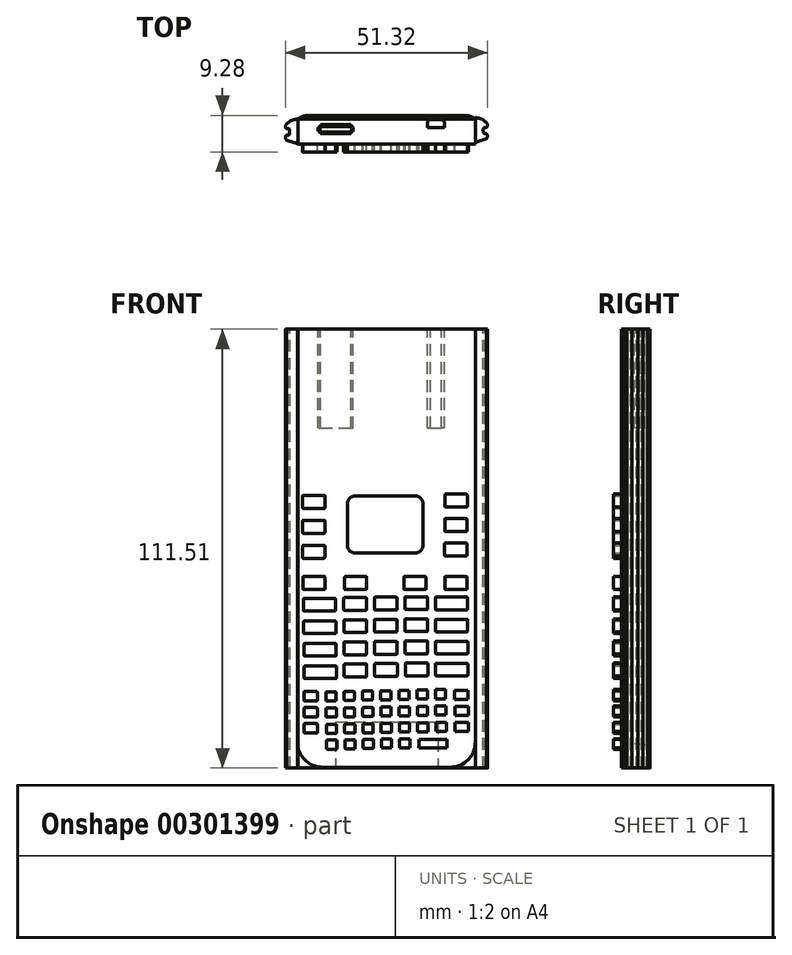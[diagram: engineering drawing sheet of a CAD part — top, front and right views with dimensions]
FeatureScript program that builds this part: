
annotation { "Feature Type Name" : "Feature", "Feature Type Description" : "" }
export const myFeature = defineFeature(function(context is Context, id is Id, definition is map)
    precondition{}
    {
        {
            var Q0;
            Q0=qCreatedBy(makeId("Front.planeOp"),FACE);
            var sketch = newSketch(context, id + "F0", { "sketchPlane" : qUnion([Q0])});
            skLineSegment(sketch, "E0.bottom", {"start": v(-48.38, 55.78) * mm, "end": v(-2.66, 55.78) * mm});
            skLineSegment(sketch, "E0.top", {"start": v(-42.03, -56.6) * mm, "end": v(-9.01, -56.6) * mm});
            skPoint(sketch, "E1.visualSharp", {"position": v(-48.38, -56.6) * mm});
            skPoint(sketch, "E2.visualSharp", {"position": v(-2.66, -56.6) * mm});
            skLineSegment(sketch, "E3.bottom", {"start": v(-36.13, -13.22) * mm, "end": v(-30.79, -13.22) * mm});
            skLineSegment(sketch, "E3.top", {"start": v(-36.13, -16.5) * mm, "end": v(-30.79, -16.5) * mm});
            skLineSegment(sketch, "E3.left", {"start": v(-36.33, -13.42) * mm, "end": v(-36.33, -16.3) * mm});
            skLineSegment(sketch, "E3.right", {"start": v(-30.59, -13.42) * mm, "end": v(-30.59, -16.3) * mm});
            skLineSegment(sketch, "E4.1.0.0", {"start": v(-28.37, -13.1) * mm, "end": v(-23.04, -13.1) * mm});
            skLineSegment(sketch, "E4.1.0.1", {"start": v(-28.57, -13.3) * mm, "end": v(-28.57, -16.2) * mm});
            skLineSegment(sketch, "E4.1.0.2", {"start": v(-28.37, -16.4) * mm, "end": v(-23.04, -16.4) * mm});
            skLineSegment(sketch, "E4.1.0.3", {"start": v(-22.83, -13.3) * mm, "end": v(-22.83, -16.2) * mm});
            skLineSegment(sketch, "E4.2.0.0", {"start": v(-20.62, -13) * mm, "end": v(-15.28, -13) * mm});
            skLineSegment(sketch, "E4.2.0.1", {"start": v(-20.82, -13.2) * mm, "end": v(-20.82, -16.08) * mm});
            skLineSegment(sketch, "E4.2.0.2", {"start": v(-20.62, -16.28) * mm, "end": v(-15.28, -16.28) * mm});
            skLineSegment(sketch, "E4.2.0.3", {"start": v(-15.08, -13.2) * mm, "end": v(-15.08, -16.08) * mm});
            skLineSegment(sketch, "E5.1.0.0", {"start": v(-30.55, -19.04) * mm, "end": v(-30.55, -21.92) * mm});
            skLineSegment(sketch, "E5.1.0.1", {"start": v(-36.1, -18.83) * mm, "end": v(-30.76, -18.83) * mm});
            skLineSegment(sketch, "E5.1.0.2", {"start": v(-36.3, -19.04) * mm, "end": v(-36.3, -21.92) * mm});
            skLineSegment(sketch, "E5.1.0.3", {"start": v(-36.1, -22.12) * mm, "end": v(-30.76, -22.12) * mm});
            skLineSegment(sketch, "E5.2.0.0", {"start": v(-30.52, -24.65) * mm, "end": v(-30.52, -27.53) * mm});
            skLineSegment(sketch, "E5.2.0.1", {"start": v(-36.06, -24.45) * mm, "end": v(-30.72, -24.45) * mm});
            skLineSegment(sketch, "E5.2.0.2", {"start": v(-36.26, -24.65) * mm, "end": v(-36.26, -27.53) * mm});
            skLineSegment(sketch, "E5.2.0.3", {"start": v(-36.06, -27.74) * mm, "end": v(-30.72, -27.74) * mm});
            skLineSegment(sketch, "E5.3.0.0", {"start": v(-30.49, -30.26) * mm, "end": v(-30.49, -33.15) * mm});
            skLineSegment(sketch, "E5.3.0.1", {"start": v(-36.03, -30.06) * mm, "end": v(-30.7, -30.06) * mm});
            skLineSegment(sketch, "E5.3.0.2", {"start": v(-36.23, -30.26) * mm, "end": v(-36.23, -33.15) * mm});
            skLineSegment(sketch, "E5.3.0.3", {"start": v(-36.03, -33.35) * mm, "end": v(-30.7, -33.35) * mm});
            skLineSegment(sketch, "E6.1.0.0", {"start": v(-28.55, -18.9) * mm, "end": v(-28.55, -21.8) * mm});
            skLineSegment(sketch, "E6.1.0.1", {"start": v(-28.35, -18.7) * mm, "end": v(-23.01, -18.7) * mm});
            skLineSegment(sketch, "E6.1.0.2", {"start": v(-22.8, -18.9) * mm, "end": v(-22.8, -21.8) * mm});
            skLineSegment(sketch, "E6.1.0.3", {"start": v(-28.35, -22) * mm, "end": v(-23.01, -22) * mm});
            skLineSegment(sketch, "E6.2.0.0", {"start": v(-20.8, -18.78) * mm, "end": v(-20.8, -21.67) * mm});
            skLineSegment(sketch, "E6.2.0.1", {"start": v(-20.6, -18.58) * mm, "end": v(-15.26, -18.58) * mm});
            skLineSegment(sketch, "E6.2.0.2", {"start": v(-15.06, -18.78) * mm, "end": v(-15.06, -21.67) * mm});
            skLineSegment(sketch, "E6.2.0.3", {"start": v(-20.6, -21.87) * mm, "end": v(-15.26, -21.87) * mm});
            skLineSegment(sketch, "E7.1.0.0", {"start": v(-22.76, -24.52) * mm, "end": v(-22.76, -27.4) * mm});
            skLineSegment(sketch, "E7.1.0.1", {"start": v(-28.3, -24.32) * mm, "end": v(-22.96, -24.32) * mm});
            skLineSegment(sketch, "E7.1.0.2", {"start": v(-28.5, -24.52) * mm, "end": v(-28.5, -27.4) * mm});
            skLineSegment(sketch, "E7.1.0.3", {"start": v(-28.3, -27.6) * mm, "end": v(-22.96, -27.6) * mm});
            skLineSegment(sketch, "E7.1.0.4", {"start": v(-22.72, -30.14) * mm, "end": v(-22.72, -33.02) * mm});
            skLineSegment(sketch, "E7.1.0.5", {"start": v(-28.26, -29.93) * mm, "end": v(-22.93, -29.93) * mm});
            skLineSegment(sketch, "E7.1.0.6", {"start": v(-28.47, -30.14) * mm, "end": v(-28.47, -33.02) * mm});
            skLineSegment(sketch, "E7.1.0.7", {"start": v(-28.26, -33.22) * mm, "end": v(-22.93, -33.22) * mm});
            skLineSegment(sketch, "E7.2.0.0", {"start": v(-15, -24.4) * mm, "end": v(-15, -27.28) * mm});
            skLineSegment(sketch, "E7.2.0.1", {"start": v(-20.53, -24.2) * mm, "end": v(-15.2, -24.2) * mm});
            skLineSegment(sketch, "E7.2.0.2", {"start": v(-20.73, -24.4) * mm, "end": v(-20.73, -27.28) * mm});
            skLineSegment(sketch, "E7.2.0.3", {"start": v(-20.53, -27.48) * mm, "end": v(-15.2, -27.48) * mm});
            skLineSegment(sketch, "E7.2.0.4", {"start": v(-14.96, -30) * mm, "end": v(-14.96, -32.9) * mm});
            skLineSegment(sketch, "E7.2.0.5", {"start": v(-20.5, -29.8) * mm, "end": v(-15.16, -29.8) * mm});
            skLineSegment(sketch, "E7.2.0.6", {"start": v(-20.7, -30) * mm, "end": v(-20.7, -32.9) * mm});
            skLineSegment(sketch, "E7.2.0.7", {"start": v(-20.5, -33.1) * mm, "end": v(-15.16, -33.1) * mm});
            skPoint(sketch, "E8.visualSharp", {"position": v(-30.59, -13.22) * mm});
            skArc(sketch, "E8.filletArc", {"start": v(-30.59, -13.42) * mm, "mid": v(-30.65, -13.28) * mm, "end": v(-30.79, -13.22) * mm});
            skPoint(sketch, "E9.visualSharp", {"position": v(-36.33, -13.22) * mm});
            skArc(sketch, "E9.filletArc", {"start": v(-36.13, -13.22) * mm, "mid": v(-36.27, -13.28) * mm, "end": v(-36.33, -13.42) * mm});
            skPoint(sketch, "E10.visualSharp", {"position": v(-36.33, -16.5) * mm});
            skArc(sketch, "E10.filletArc", {"start": v(-36.33, -16.3) * mm, "mid": v(-36.27, -16.45) * mm, "end": v(-36.13, -16.5) * mm});
            skPoint(sketch, "E11.visualSharp", {"position": v(-30.59, -16.5) * mm});
            skArc(sketch, "E11.filletArc", {"start": v(-30.79, -16.5) * mm, "mid": v(-30.65, -16.45) * mm, "end": v(-30.59, -16.3) * mm});
            skPoint(sketch, "E12.visualSharp", {"position": v(-28.57, -13.1) * mm});
            skArc(sketch, "E12.filletArc", {"start": v(-28.37, -13.1) * mm, "mid": v(-28.52, -13.17) * mm, "end": v(-28.57, -13.3) * mm});
            skPoint(sketch, "E13.visualSharp", {"position": v(-22.83, -13.1) * mm});
            skArc(sketch, "E13.filletArc", {"start": v(-22.83, -13.3) * mm, "mid": v(-22.9, -13.17) * mm, "end": v(-23.04, -13.1) * mm});
            skPoint(sketch, "E14.visualSharp", {"position": v(-22.83, -16.4) * mm});
            skArc(sketch, "E14.filletArc", {"start": v(-23.04, -16.4) * mm, "mid": v(-22.9, -16.34) * mm, "end": v(-22.83, -16.2) * mm});
            skPoint(sketch, "E15.visualSharp", {"position": v(-28.57, -16.4) * mm});
            skArc(sketch, "E15.filletArc", {"start": v(-28.57, -16.2) * mm, "mid": v(-28.52, -16.34) * mm, "end": v(-28.37, -16.4) * mm});
            skPoint(sketch, "E16.visualSharp", {"position": v(-20.82, -13) * mm});
            skArc(sketch, "E16.filletArc", {"start": v(-20.62, -13) * mm, "mid": v(-20.76, -13.05) * mm, "end": v(-20.82, -13.2) * mm});
            skPoint(sketch, "E17.visualSharp", {"position": v(-15.08, -13) * mm});
            skArc(sketch, "E17.filletArc", {"start": v(-15.08, -13.2) * mm, "mid": v(-15.14, -13.05) * mm, "end": v(-15.28, -13) * mm});
            skPoint(sketch, "E18.visualSharp", {"position": v(-15.08, -16.28) * mm});
            skArc(sketch, "E18.filletArc", {"start": v(-15.28, -16.28) * mm, "mid": v(-15.14, -16.22) * mm, "end": v(-15.08, -16.08) * mm});
            skPoint(sketch, "E19.visualSharp", {"position": v(-20.82, -16.28) * mm});
            skArc(sketch, "E19.filletArc", {"start": v(-20.82, -16.08) * mm, "mid": v(-20.76, -16.22) * mm, "end": v(-20.62, -16.28) * mm});
            skPoint(sketch, "E20.visualSharp", {"position": v(-15.06, -18.58) * mm});
            skArc(sketch, "E20.filletArc", {"start": v(-15.06, -18.78) * mm, "mid": v(-15.12, -18.64) * mm, "end": v(-15.26, -18.58) * mm});
            skPoint(sketch, "E21.visualSharp", {"position": v(-15.06, -21.87) * mm});
            skArc(sketch, "E21.filletArc", {"start": v(-15.26, -21.87) * mm, "mid": v(-15.12, -21.81) * mm, "end": v(-15.06, -21.67) * mm});
            skPoint(sketch, "E22.visualSharp", {"position": v(-20.8, -21.87) * mm});
            skArc(sketch, "E22.filletArc", {"start": v(-20.8, -21.67) * mm, "mid": v(-20.74, -21.81) * mm, "end": v(-20.6, -21.87) * mm});
            skPoint(sketch, "E23.visualSharp", {"position": v(-20.8, -18.58) * mm});
            skArc(sketch, "E23.filletArc", {"start": v(-20.6, -18.58) * mm, "mid": v(-20.74, -18.64) * mm, "end": v(-20.8, -18.78) * mm});
            skPoint(sketch, "E24.visualSharp", {"position": v(-22.8, -18.7) * mm});
            skArc(sketch, "E24.filletArc", {"start": v(-22.8, -18.9) * mm, "mid": v(-22.87, -18.77) * mm, "end": v(-23.01, -18.7) * mm});
            skPoint(sketch, "E25.visualSharp", {"position": v(-22.8, -22) * mm});
            skArc(sketch, "E25.filletArc", {"start": v(-23.01, -22) * mm, "mid": v(-22.87, -21.94) * mm, "end": v(-22.8, -21.8) * mm});
            skPoint(sketch, "E26.visualSharp", {"position": v(-28.55, -22) * mm});
            skArc(sketch, "E26.filletArc", {"start": v(-28.55, -21.8) * mm, "mid": v(-28.5, -21.94) * mm, "end": v(-28.35, -22) * mm});
            skPoint(sketch, "E27.visualSharp", {"position": v(-28.55, -18.7) * mm});
            skArc(sketch, "E27.filletArc", {"start": v(-28.35, -18.7) * mm, "mid": v(-28.5, -18.77) * mm, "end": v(-28.55, -18.9) * mm});
            skPoint(sketch, "E28.visualSharp", {"position": v(-30.55, -18.83) * mm});
            skArc(sketch, "E28.filletArc", {"start": v(-30.55, -19.04) * mm, "mid": v(-30.61, -18.9) * mm, "end": v(-30.76, -18.83) * mm});
            skPoint(sketch, "E29.visualSharp", {"position": v(-30.55, -22.12) * mm});
            skArc(sketch, "E29.filletArc", {"start": v(-30.76, -22.12) * mm, "mid": v(-30.61, -22.06) * mm, "end": v(-30.55, -21.92) * mm});
            skPoint(sketch, "E30.visualSharp", {"position": v(-36.3, -22.12) * mm});
            skArc(sketch, "E30.filletArc", {"start": v(-36.3, -21.92) * mm, "mid": v(-36.24, -22.06) * mm, "end": v(-36.1, -22.12) * mm});
            skPoint(sketch, "E31.visualSharp", {"position": v(-36.3, -18.83) * mm});
            skArc(sketch, "E31.filletArc", {"start": v(-36.1, -18.83) * mm, "mid": v(-36.24, -18.9) * mm, "end": v(-36.3, -19.04) * mm});
            skPoint(sketch, "E32.visualSharp", {"position": v(-36.26, -24.45) * mm});
            skArc(sketch, "E32.filletArc", {"start": v(-36.06, -24.45) * mm, "mid": v(-36.2, -24.5) * mm, "end": v(-36.26, -24.65) * mm});
            skPoint(sketch, "E33.visualSharp", {"position": v(-36.26, -27.74) * mm});
            skArc(sketch, "E33.filletArc", {"start": v(-36.26, -27.53) * mm, "mid": v(-36.2, -27.68) * mm, "end": v(-36.06, -27.74) * mm});
            skPoint(sketch, "E34.visualSharp", {"position": v(-30.52, -27.74) * mm});
            skArc(sketch, "E34.filletArc", {"start": v(-30.72, -27.74) * mm, "mid": v(-30.58, -27.68) * mm, "end": v(-30.52, -27.53) * mm});
            skPoint(sketch, "E35.visualSharp", {"position": v(-30.52, -24.45) * mm});
            skArc(sketch, "E35.filletArc", {"start": v(-30.52, -24.65) * mm, "mid": v(-30.58, -24.5) * mm, "end": v(-30.72, -24.45) * mm});
            skPoint(sketch, "E36.visualSharp", {"position": v(-28.5, -24.32) * mm});
            skArc(sketch, "E36.filletArc", {"start": v(-28.3, -24.32) * mm, "mid": v(-28.44, -24.38) * mm, "end": v(-28.5, -24.52) * mm});
            skPoint(sketch, "E37.visualSharp", {"position": v(-22.76, -24.32) * mm});
            skArc(sketch, "E37.filletArc", {"start": v(-22.76, -24.52) * mm, "mid": v(-22.82, -24.38) * mm, "end": v(-22.96, -24.32) * mm});
            skPoint(sketch, "E38.visualSharp", {"position": v(-28.5, -27.6) * mm});
            skArc(sketch, "E38.filletArc", {"start": v(-28.5, -27.4) * mm, "mid": v(-28.44, -27.55) * mm, "end": v(-28.3, -27.6) * mm});
            skPoint(sketch, "E39.visualSharp", {"position": v(-36.23, -30.06) * mm});
            skArc(sketch, "E39.filletArc", {"start": v(-36.03, -30.06) * mm, "mid": v(-36.17, -30.12) * mm, "end": v(-36.23, -30.26) * mm});
            skPoint(sketch, "E40.visualSharp", {"position": v(-36.23, -33.35) * mm});
            skArc(sketch, "E40.filletArc", {"start": v(-36.23, -33.15) * mm, "mid": v(-36.17, -33.3) * mm, "end": v(-36.03, -33.35) * mm});
            skPoint(sketch, "E41.visualSharp", {"position": v(-30.49, -33.35) * mm});
            skArc(sketch, "E41.filletArc", {"start": v(-30.7, -33.35) * mm, "mid": v(-30.55, -33.3) * mm, "end": v(-30.49, -33.15) * mm});
            skPoint(sketch, "E42.visualSharp", {"position": v(-30.49, -30.06) * mm});
            skArc(sketch, "E42.filletArc", {"start": v(-30.49, -30.26) * mm, "mid": v(-30.55, -30.12) * mm, "end": v(-30.7, -30.06) * mm});
            skPoint(sketch, "E43.visualSharp", {"position": v(-28.47, -29.93) * mm});
            skArc(sketch, "E43.filletArc", {"start": v(-28.26, -29.93) * mm, "mid": v(-28.4, -30) * mm, "end": v(-28.47, -30.14) * mm});
            skPoint(sketch, "E44.visualSharp", {"position": v(-28.47, -33.22) * mm});
            skArc(sketch, "E44.filletArc", {"start": v(-28.47, -33.02) * mm, "mid": v(-28.4, -33.16) * mm, "end": v(-28.26, -33.22) * mm});
            skPoint(sketch, "E45.visualSharp", {"position": v(-22.72, -29.93) * mm});
            skArc(sketch, "E45.filletArc", {"start": v(-22.72, -30.14) * mm, "mid": v(-22.78, -30) * mm, "end": v(-22.93, -29.93) * mm});
            skPoint(sketch, "E46.visualSharp", {"position": v(-20.7, -29.8) * mm});
            skArc(sketch, "E46.filletArc", {"start": v(-20.5, -29.8) * mm, "mid": v(-20.64, -29.87) * mm, "end": v(-20.7, -30) * mm});
            skPoint(sketch, "E47.visualSharp", {"position": v(-14.96, -29.8) * mm});
            skArc(sketch, "E47.filletArc", {"start": v(-14.96, -30) * mm, "mid": v(-15.02, -29.87) * mm, "end": v(-15.16, -29.8) * mm});
            skPoint(sketch, "E48.visualSharp", {"position": v(-14.96, -33.1) * mm});
            skArc(sketch, "E48.filletArc", {"start": v(-15.16, -33.1) * mm, "mid": v(-15.02, -33.04) * mm, "end": v(-14.96, -32.9) * mm});
            skPoint(sketch, "E49.visualSharp", {"position": v(-20.7, -33.1) * mm});
            skArc(sketch, "E49.filletArc", {"start": v(-20.7, -32.9) * mm, "mid": v(-20.64, -33.04) * mm, "end": v(-20.5, -33.1) * mm});
            skPoint(sketch, "E50.visualSharp", {"position": v(-20.73, -27.48) * mm});
            skArc(sketch, "E50.filletArc", {"start": v(-20.73, -27.28) * mm, "mid": v(-20.67, -27.42) * mm, "end": v(-20.53, -27.48) * mm});
            skPoint(sketch, "E51.visualSharp", {"position": v(-20.73, -24.2) * mm});
            skArc(sketch, "E51.filletArc", {"start": v(-20.53, -24.2) * mm, "mid": v(-20.67, -24.25) * mm, "end": v(-20.73, -24.4) * mm});
            skPoint(sketch, "E52.visualSharp", {"position": v(-15, -24.2) * mm});
            skArc(sketch, "E52.filletArc", {"start": v(-15, -24.4) * mm, "mid": v(-15.05, -24.25) * mm, "end": v(-15.2, -24.2) * mm});
            skPoint(sketch, "E53.visualSharp", {"position": v(-15, -27.48) * mm});
            skArc(sketch, "E53.filletArc", {"start": v(-15.2, -27.48) * mm, "mid": v(-15.05, -27.42) * mm, "end": v(-15, -27.28) * mm});
            skPoint(sketch, "E54.visualSharp", {"position": v(-22.76, -27.6) * mm});
            skArc(sketch, "E54.filletArc", {"start": v(-22.96, -27.6) * mm, "mid": v(-22.82, -27.55) * mm, "end": v(-22.76, -27.4) * mm});
            skPoint(sketch, "E55.visualSharp", {"position": v(-22.72, -33.22) * mm});
            skArc(sketch, "E55.filletArc", {"start": v(-22.93, -33.22) * mm, "mid": v(-22.78, -33.16) * mm, "end": v(-22.72, -33.02) * mm});
            skLineSegment(sketch, "E56.bottom", {"start": v(-46.4, -13.46) * mm, "end": v(-38.59, -13.46) * mm});
            skLineSegment(sketch, "E56.top", {"start": v(-46.4, -16.64) * mm, "end": v(-38.59, -16.64) * mm});
            skLineSegment(sketch, "E56.left", {"start": v(-46.6, -13.66) * mm, "end": v(-46.6, -16.44) * mm});
            skLineSegment(sketch, "E56.right", {"start": v(-38.39, -13.66) * mm, "end": v(-38.39, -16.44) * mm});
            skLineSegment(sketch, "E57.1.0.0", {"start": v(-46.33, -19.18) * mm, "end": v(-38.51, -19.18) * mm});
            skLineSegment(sketch, "E57.1.0.1", {"start": v(-46.53, -19.38) * mm, "end": v(-46.53, -22.16) * mm});
            skLineSegment(sketch, "E57.1.0.2", {"start": v(-46.33, -22.36) * mm, "end": v(-38.51, -22.36) * mm});
            skLineSegment(sketch, "E57.1.0.3", {"start": v(-38.31, -19.38) * mm, "end": v(-38.31, -22.16) * mm});
            skLineSegment(sketch, "E57.2.0.0", {"start": v(-46.25, -24.9) * mm, "end": v(-38.44, -24.9) * mm});
            skLineSegment(sketch, "E57.2.0.1", {"start": v(-46.46, -25.1) * mm, "end": v(-46.46, -27.88) * mm});
            skLineSegment(sketch, "E57.2.0.2", {"start": v(-46.25, -28.08) * mm, "end": v(-38.44, -28.08) * mm});
            skLineSegment(sketch, "E57.2.0.3", {"start": v(-38.23, -25.1) * mm, "end": v(-38.23, -27.88) * mm});
            skLineSegment(sketch, "E57.3.0.0", {"start": v(-46.18, -30.61) * mm, "end": v(-38.36, -30.61) * mm});
            skLineSegment(sketch, "E57.3.0.1", {"start": v(-46.38, -30.82) * mm, "end": v(-46.38, -33.6) * mm});
            skLineSegment(sketch, "E57.3.0.2", {"start": v(-46.18, -33.8) * mm, "end": v(-38.36, -33.8) * mm});
            skLineSegment(sketch, "E57.3.0.3", {"start": v(-38.16, -30.82) * mm, "end": v(-38.16, -33.6) * mm});
            skLineSegment(sketch, "E58.1.0.0", {"start": v(-12.88, -13.1) * mm, "end": v(-5.06, -13.1) * mm});
            skLineSegment(sketch, "E58.1.0.1", {"start": v(-13.08, -13.3) * mm, "end": v(-13.08, -16.09) * mm});
            skLineSegment(sketch, "E58.1.0.2", {"start": v(-12.88, -16.3) * mm, "end": v(-5.06, -16.3) * mm});
            skLineSegment(sketch, "E58.1.0.3", {"start": v(-4.86, -13.3) * mm, "end": v(-4.86, -16.09) * mm});
            skLineSegment(sketch, "E59.1.0.0", {"start": v(-13.06, -18.91) * mm, "end": v(-13.06, -21.7) * mm});
            skLineSegment(sketch, "E59.1.0.1", {"start": v(-12.85, -18.7) * mm, "end": v(-5.04, -18.7) * mm});
            skLineSegment(sketch, "E59.1.0.2", {"start": v(-4.83, -18.91) * mm, "end": v(-4.83, -21.7) * mm});
            skLineSegment(sketch, "E59.1.0.3", {"start": v(-12.85, -21.9) * mm, "end": v(-5.04, -21.9) * mm});
            skLineSegment(sketch, "E59.2.0.0", {"start": v(-13.03, -24.52) * mm, "end": v(-13.03, -27.3) * mm});
            skLineSegment(sketch, "E59.2.0.1", {"start": v(-12.83, -24.31) * mm, "end": v(-5.01, -24.31) * mm});
            skLineSegment(sketch, "E59.2.0.2", {"start": v(-4.8, -24.52) * mm, "end": v(-4.8, -27.3) * mm});
            skLineSegment(sketch, "E59.2.0.3", {"start": v(-12.83, -27.5) * mm, "end": v(-5.01, -27.5) * mm});
            skLineSegment(sketch, "E59.3.0.0", {"start": v(-13, -30.12) * mm, "end": v(-13, -32.9) * mm});
            skLineSegment(sketch, "E59.3.0.1", {"start": v(-12.8, -29.92) * mm, "end": v(-4.99, -29.92) * mm});
            skLineSegment(sketch, "E59.3.0.2", {"start": v(-4.78, -30.12) * mm, "end": v(-4.78, -32.9) * mm});
            skLineSegment(sketch, "E59.3.0.3", {"start": v(-12.8, -33.1) * mm, "end": v(-4.99, -33.1) * mm});
            skPoint(sketch, "E60.visualSharp", {"position": v(-13.08, -13.1) * mm});
            skArc(sketch, "E60.filletArc", {"start": v(-12.88, -13.1) * mm, "mid": v(-13.02, -13.17) * mm, "end": v(-13.08, -13.3) * mm});
            skPoint(sketch, "E61.visualSharp", {"position": v(-4.86, -13.1) * mm});
            skArc(sketch, "E61.filletArc", {"start": v(-4.86, -13.3) * mm, "mid": v(-4.92, -13.17) * mm, "end": v(-5.06, -13.1) * mm});
            skPoint(sketch, "E62.visualSharp", {"position": v(-4.86, -16.3) * mm});
            skArc(sketch, "E62.filletArc", {"start": v(-5.06, -16.3) * mm, "mid": v(-4.92, -16.23) * mm, "end": v(-4.86, -16.09) * mm});
            skPoint(sketch, "E63.visualSharp", {"position": v(-13.08, -16.3) * mm});
            skArc(sketch, "E63.filletArc", {"start": v(-13.08, -16.09) * mm, "mid": v(-13.02, -16.23) * mm, "end": v(-12.88, -16.3) * mm});
            skPoint(sketch, "E64.visualSharp", {"position": v(-13.06, -18.7) * mm});
            skArc(sketch, "E64.filletArc", {"start": v(-12.85, -18.7) * mm, "mid": v(-13, -18.77) * mm, "end": v(-13.06, -18.91) * mm});
            skPoint(sketch, "E65.visualSharp", {"position": v(-13.06, -21.9) * mm});
            skArc(sketch, "E65.filletArc", {"start": v(-13.06, -21.7) * mm, "mid": v(-13, -21.84) * mm, "end": v(-12.85, -21.9) * mm});
            skPoint(sketch, "E66.visualSharp", {"position": v(-4.83, -21.9) * mm});
            skArc(sketch, "E66.filletArc", {"start": v(-5.04, -21.9) * mm, "mid": v(-4.9, -21.84) * mm, "end": v(-4.83, -21.7) * mm});
            skPoint(sketch, "E67.visualSharp", {"position": v(-4.83, -18.7) * mm});
            skArc(sketch, "E67.filletArc", {"start": v(-4.83, -18.91) * mm, "mid": v(-4.9, -18.77) * mm, "end": v(-5.04, -18.7) * mm});
            skPoint(sketch, "E68.visualSharp", {"position": v(-4.8, -24.31) * mm});
            skArc(sketch, "E68.filletArc", {"start": v(-4.8, -24.52) * mm, "mid": v(-4.87, -24.37) * mm, "end": v(-5.01, -24.31) * mm});
            skPoint(sketch, "E69.visualSharp", {"position": v(-13.03, -24.31) * mm});
            skArc(sketch, "E69.filletArc", {"start": v(-12.83, -24.31) * mm, "mid": v(-12.97, -24.37) * mm, "end": v(-13.03, -24.52) * mm});
            skPoint(sketch, "E70.visualSharp", {"position": v(-13.03, -27.5) * mm});
            skArc(sketch, "E70.filletArc", {"start": v(-13.03, -27.3) * mm, "mid": v(-12.97, -27.44) * mm, "end": v(-12.83, -27.5) * mm});
            skPoint(sketch, "E71.visualSharp", {"position": v(-4.8, -27.5) * mm});
            skArc(sketch, "E71.filletArc", {"start": v(-5.01, -27.5) * mm, "mid": v(-4.87, -27.44) * mm, "end": v(-4.8, -27.3) * mm});
            skPoint(sketch, "E72.visualSharp", {"position": v(-4.78, -29.92) * mm});
            skArc(sketch, "E72.filletArc", {"start": v(-4.78, -30.12) * mm, "mid": v(-4.84, -29.98) * mm, "end": v(-4.99, -29.92) * mm});
            skPoint(sketch, "E73.visualSharp", {"position": v(-13, -29.92) * mm});
            skArc(sketch, "E73.filletArc", {"start": v(-12.8, -29.92) * mm, "mid": v(-12.95, -29.98) * mm, "end": v(-13, -30.12) * mm});
            skPoint(sketch, "E74.visualSharp", {"position": v(-4.78, -33.1) * mm});
            skArc(sketch, "E74.filletArc", {"start": v(-4.99, -33.1) * mm, "mid": v(-4.84, -33.04) * mm, "end": v(-4.78, -32.9) * mm});
            skPoint(sketch, "E75.visualSharp", {"position": v(-13, -33.1) * mm});
            skArc(sketch, "E75.filletArc", {"start": v(-13, -32.9) * mm, "mid": v(-12.95, -33.04) * mm, "end": v(-12.8, -33.1) * mm});
            skPoint(sketch, "E76.visualSharp", {"position": v(-46.6, -13.46) * mm});
            skArc(sketch, "E76.filletArc", {"start": v(-46.4, -13.46) * mm, "mid": v(-46.55, -13.52) * mm, "end": v(-46.6, -13.66) * mm});
            skPoint(sketch, "E77.visualSharp", {"position": v(-38.39, -13.46) * mm});
            skArc(sketch, "E77.filletArc", {"start": v(-38.39, -13.66) * mm, "mid": v(-38.45, -13.52) * mm, "end": v(-38.59, -13.46) * mm});
            skPoint(sketch, "E78.visualSharp", {"position": v(-38.39, -16.64) * mm});
            skArc(sketch, "E78.filletArc", {"start": v(-38.59, -16.64) * mm, "mid": v(-38.45, -16.58) * mm, "end": v(-38.39, -16.44) * mm});
            skPoint(sketch, "E79.visualSharp", {"position": v(-46.53, -19.18) * mm});
            skArc(sketch, "E79.filletArc", {"start": v(-46.33, -19.18) * mm, "mid": v(-46.47, -19.24) * mm, "end": v(-46.53, -19.38) * mm});
            skPoint(sketch, "E80.visualSharp", {"position": v(-46.6, -16.64) * mm});
            skArc(sketch, "E80.filletArc", {"start": v(-46.6, -16.44) * mm, "mid": v(-46.55, -16.58) * mm, "end": v(-46.4, -16.64) * mm});
            skPoint(sketch, "E81.visualSharp", {"position": v(-38.31, -19.18) * mm});
            skArc(sketch, "E81.filletArc", {"start": v(-38.31, -19.38) * mm, "mid": v(-38.37, -19.24) * mm, "end": v(-38.51, -19.18) * mm});
            skPoint(sketch, "E82.visualSharp", {"position": v(-38.31, -22.36) * mm});
            skArc(sketch, "E82.filletArc", {"start": v(-38.51, -22.36) * mm, "mid": v(-38.37, -22.3) * mm, "end": v(-38.31, -22.16) * mm});
            skPoint(sketch, "E83.visualSharp", {"position": v(-46.53, -22.36) * mm});
            skArc(sketch, "E83.filletArc", {"start": v(-46.53, -22.16) * mm, "mid": v(-46.47, -22.3) * mm, "end": v(-46.33, -22.36) * mm});
            skPoint(sketch, "E84.visualSharp", {"position": v(-46.46, -24.9) * mm});
            skArc(sketch, "E84.filletArc", {"start": v(-46.25, -24.9) * mm, "mid": v(-46.4, -24.96) * mm, "end": v(-46.46, -25.1) * mm});
            skPoint(sketch, "E85.visualSharp", {"position": v(-38.23, -24.9) * mm});
            skArc(sketch, "E85.filletArc", {"start": v(-38.23, -25.1) * mm, "mid": v(-38.3, -24.96) * mm, "end": v(-38.44, -24.9) * mm});
            skPoint(sketch, "E86.visualSharp", {"position": v(-38.23, -28.08) * mm});
            skArc(sketch, "E86.filletArc", {"start": v(-38.44, -28.08) * mm, "mid": v(-38.3, -28.02) * mm, "end": v(-38.23, -27.88) * mm});
            skPoint(sketch, "E87.visualSharp", {"position": v(-46.46, -28.08) * mm});
            skArc(sketch, "E87.filletArc", {"start": v(-46.46, -27.88) * mm, "mid": v(-46.4, -28.02) * mm, "end": v(-46.25, -28.08) * mm});
            skPoint(sketch, "E88.visualSharp", {"position": v(-46.38, -30.61) * mm});
            skArc(sketch, "E88.filletArc", {"start": v(-46.18, -30.61) * mm, "mid": v(-46.32, -30.67) * mm, "end": v(-46.38, -30.82) * mm});
            skPoint(sketch, "E89.visualSharp", {"position": v(-38.16, -30.61) * mm});
            skArc(sketch, "E89.filletArc", {"start": v(-38.16, -30.82) * mm, "mid": v(-38.22, -30.67) * mm, "end": v(-38.36, -30.61) * mm});
            skPoint(sketch, "E90.visualSharp", {"position": v(-38.16, -33.8) * mm});
            skArc(sketch, "E90.filletArc", {"start": v(-38.36, -33.8) * mm, "mid": v(-38.22, -33.74) * mm, "end": v(-38.16, -33.6) * mm});
            skPoint(sketch, "E91.visualSharp", {"position": v(-46.38, -33.8) * mm});
            skArc(sketch, "E91.filletArc", {"start": v(-46.38, -33.6) * mm, "mid": v(-46.32, -33.74) * mm, "end": v(-46.18, -33.8) * mm});
            skLineSegment(sketch, "E92.bottom", {"start": v(-46.58, 12.78) * mm, "end": v(-41.3, 12.78) * mm});
            skLineSegment(sketch, "E92.top", {"start": v(-46.58, 9.49) * mm, "end": v(-41.3, 9.49) * mm});
            skLineSegment(sketch, "E92.left", {"start": v(-46.79, 12.58) * mm, "end": v(-46.79, 9.7) * mm});
            skLineSegment(sketch, "E92.right", {"start": v(-41.1, 12.58) * mm, "end": v(-41.1, 9.7) * mm});
            skLineSegment(sketch, "E93.1.0.0", {"start": v(-41.12, 6.23) * mm, "end": v(-41.12, 3.34) * mm});
            skLineSegment(sketch, "E93.1.0.1", {"start": v(-46.61, 6.43) * mm, "end": v(-41.33, 6.43) * mm});
            skLineSegment(sketch, "E93.1.0.2", {"start": v(-46.81, 6.23) * mm, "end": v(-46.81, 3.34) * mm});
            skLineSegment(sketch, "E93.1.0.3", {"start": v(-46.61, 3.14) * mm, "end": v(-41.33, 3.14) * mm});
            skLineSegment(sketch, "E93.2.0.0", {"start": v(-41.15, -0.12) * mm, "end": v(-41.15, -3) * mm});
            skLineSegment(sketch, "E93.2.0.1", {"start": v(-46.64, 0.08) * mm, "end": v(-41.35, 0.08) * mm});
            skLineSegment(sketch, "E93.2.0.2", {"start": v(-46.84, -0.12) * mm, "end": v(-46.84, -3) * mm});
            skLineSegment(sketch, "E93.2.0.3", {"start": v(-46.64, -3.21) * mm, "end": v(-41.35, -3.21) * mm});
            skLineSegment(sketch, "E94.1.0.0", {"start": v(-10.44, 13.06) * mm, "end": v(-5.16, 13.06) * mm});
            skLineSegment(sketch, "E94.1.0.1", {"start": v(-10.64, 12.85) * mm, "end": v(-10.64, 9.96) * mm});
            skLineSegment(sketch, "E94.1.0.2", {"start": v(-10.44, 9.76) * mm, "end": v(-5.16, 9.76) * mm});
            skLineSegment(sketch, "E94.1.0.3", {"start": v(-4.95, 12.85) * mm, "end": v(-4.95, 9.96) * mm});
            skLineSegment(sketch, "E95.1.0.0", {"start": v(-10.67, 6.65) * mm, "end": v(-10.67, 3.76) * mm});
            skLineSegment(sketch, "E95.1.0.1", {"start": v(-10.46, 6.85) * mm, "end": v(-5.18, 6.85) * mm});
            skLineSegment(sketch, "E95.1.0.2", {"start": v(-4.98, 6.65) * mm, "end": v(-4.98, 3.76) * mm});
            skLineSegment(sketch, "E95.1.0.3", {"start": v(-10.46, 3.56) * mm, "end": v(-5.18, 3.56) * mm});
            skLineSegment(sketch, "E95.2.0.0", {"start": v(-10.7, 0.44) * mm, "end": v(-10.7, -2.44) * mm});
            skLineSegment(sketch, "E95.2.0.1", {"start": v(-10.5, 0.65) * mm, "end": v(-5.2, 0.65) * mm});
            skLineSegment(sketch, "E95.2.0.2", {"start": v(-5, 0.44) * mm, "end": v(-5, -2.44) * mm});
            skLineSegment(sketch, "E95.2.0.3", {"start": v(-10.5, -2.65) * mm, "end": v(-5.2, -2.65) * mm});
            skLineSegment(sketch, "E96.1.0.0", {"start": v(-10.46, -7.87) * mm, "end": v(-5.18, -7.87) * mm});
            skLineSegment(sketch, "E96.1.0.1", {"start": v(-10.67, -8.08) * mm, "end": v(-10.67, -10.97) * mm});
            skLineSegment(sketch, "E96.1.0.2", {"start": v(-10.46, -11.17) * mm, "end": v(-5.18, -11.17) * mm});
            skLineSegment(sketch, "E96.1.0.3", {"start": v(-4.98, -8.08) * mm, "end": v(-4.98, -10.97) * mm});
            skLineSegment(sketch, "E97.1.0.0", {"start": v(-21.08, -8.08) * mm, "end": v(-21.08, -10.97) * mm});
            skLineSegment(sketch, "E97.1.0.1", {"start": v(-20.88, -7.88) * mm, "end": v(-15.6, -7.88) * mm});
            skLineSegment(sketch, "E97.1.0.2", {"start": v(-15.4, -8.08) * mm, "end": v(-15.4, -10.97) * mm});
            skLineSegment(sketch, "E97.1.0.3", {"start": v(-20.88, -11.18) * mm, "end": v(-15.6, -11.18) * mm});
            skLineSegment(sketch, "E98.1.0.0", {"start": v(-46.53, -7.87) * mm, "end": v(-41.25, -7.87) * mm});
            skLineSegment(sketch, "E98.1.0.1", {"start": v(-46.53, -11.17) * mm, "end": v(-41.25, -11.17) * mm});
            skLineSegment(sketch, "E98.1.0.2", {"start": v(-41.05, -8.08) * mm, "end": v(-41.05, -10.97) * mm});
            skLineSegment(sketch, "E98.1.0.3", {"start": v(-46.74, -8.08) * mm, "end": v(-46.74, -10.97) * mm});
            skLineSegment(sketch, "E99.1.0.0", {"start": v(-30.48, -8.08) * mm, "end": v(-30.48, -10.97) * mm});
            skLineSegment(sketch, "E99.1.0.1", {"start": v(-35.97, -7.88) * mm, "end": v(-30.68, -7.88) * mm});
            skLineSegment(sketch, "E99.1.0.2", {"start": v(-36.17, -8.08) * mm, "end": v(-36.17, -10.97) * mm});
            skLineSegment(sketch, "E99.1.0.3", {"start": v(-35.97, -11.18) * mm, "end": v(-30.68, -11.18) * mm});
            skPoint(sketch, "E100.visualSharp", {"position": v(-46.79, 12.78) * mm});
            skArc(sketch, "E100.filletArc", {"start": v(-46.58, 12.78) * mm, "mid": v(-46.73, 12.72) * mm, "end": v(-46.79, 12.58) * mm});
            skPoint(sketch, "E101.visualSharp", {"position": v(-41.1, 12.78) * mm});
            skArc(sketch, "E101.filletArc", {"start": v(-41.1, 12.58) * mm, "mid": v(-41.16, 12.72) * mm, "end": v(-41.3, 12.78) * mm});
            skPoint(sketch, "E102.visualSharp", {"position": v(-46.79, 9.49) * mm});
            skArc(sketch, "E102.filletArc", {"start": v(-46.79, 9.7) * mm, "mid": v(-46.73, 9.55) * mm, "end": v(-46.58, 9.49) * mm});
            skPoint(sketch, "E103.visualSharp", {"position": v(-41.1, 9.49) * mm});
            skArc(sketch, "E103.filletArc", {"start": v(-41.3, 9.49) * mm, "mid": v(-41.16, 9.55) * mm, "end": v(-41.1, 9.7) * mm});
            skPoint(sketch, "E104.visualSharp", {"position": v(-41.12, 6.43) * mm});
            skArc(sketch, "E104.filletArc", {"start": v(-41.12, 6.23) * mm, "mid": v(-41.18, 6.38) * mm, "end": v(-41.33, 6.43) * mm});
            skPoint(sketch, "E105.visualSharp", {"position": v(-46.81, 6.43) * mm});
            skArc(sketch, "E105.filletArc", {"start": v(-46.61, 6.43) * mm, "mid": v(-46.75, 6.38) * mm, "end": v(-46.81, 6.23) * mm});
            skPoint(sketch, "E106.visualSharp", {"position": v(-46.81, 3.14) * mm});
            skArc(sketch, "E106.filletArc", {"start": v(-46.81, 3.34) * mm, "mid": v(-46.75, 3.2) * mm, "end": v(-46.61, 3.14) * mm});
            skPoint(sketch, "E107.visualSharp", {"position": v(-41.12, 3.14) * mm});
            skArc(sketch, "E107.filletArc", {"start": v(-41.33, 3.14) * mm, "mid": v(-41.18, 3.2) * mm, "end": v(-41.12, 3.34) * mm});
            skPoint(sketch, "E108.visualSharp", {"position": v(-41.15, 0.08) * mm});
            skArc(sketch, "E108.filletArc", {"start": v(-41.15, -0.12) * mm, "mid": v(-41.2, 0.03) * mm, "end": v(-41.35, 0.08) * mm});
            skPoint(sketch, "E109.visualSharp", {"position": v(-46.84, 0.08) * mm});
            skArc(sketch, "E109.filletArc", {"start": v(-46.64, 0.08) * mm, "mid": v(-46.78, 0.03) * mm, "end": v(-46.84, -0.12) * mm});
            skPoint(sketch, "E110.visualSharp", {"position": v(-46.84, -3.21) * mm});
            skArc(sketch, "E110.filletArc", {"start": v(-46.84, -3) * mm, "mid": v(-46.78, -3.15) * mm, "end": v(-46.64, -3.21) * mm});
            skPoint(sketch, "E111.visualSharp", {"position": v(-41.15, -3.21) * mm});
            skArc(sketch, "E111.filletArc", {"start": v(-41.35, -3.21) * mm, "mid": v(-41.2, -3.15) * mm, "end": v(-41.15, -3) * mm});
            skPoint(sketch, "E112.visualSharp", {"position": v(-41.05, -7.87) * mm});
            skArc(sketch, "E112.filletArc", {"start": v(-41.05, -8.08) * mm, "mid": v(-41.1, -7.93) * mm, "end": v(-41.25, -7.87) * mm});
            skPoint(sketch, "E113.visualSharp", {"position": v(-41.05, -11.17) * mm});
            skArc(sketch, "E113.filletArc", {"start": v(-41.25, -11.17) * mm, "mid": v(-41.1, -11.11) * mm, "end": v(-41.05, -10.97) * mm});
            skPoint(sketch, "E114.visualSharp", {"position": v(-46.74, -11.17) * mm});
            skArc(sketch, "E114.filletArc", {"start": v(-46.74, -10.97) * mm, "mid": v(-46.68, -11.11) * mm, "end": v(-46.53, -11.17) * mm});
            skPoint(sketch, "E115.visualSharp", {"position": v(-46.74, -7.87) * mm});
            skArc(sketch, "E115.filletArc", {"start": v(-46.53, -7.87) * mm, "mid": v(-46.68, -7.93) * mm, "end": v(-46.74, -8.08) * mm});
            skPoint(sketch, "E116.visualSharp", {"position": v(-36.17, -7.88) * mm});
            skArc(sketch, "E116.filletArc", {"start": v(-35.97, -7.88) * mm, "mid": v(-36.11, -7.94) * mm, "end": v(-36.17, -8.08) * mm});
            skPoint(sketch, "E117.visualSharp", {"position": v(-30.48, -11.18) * mm});
            skArc(sketch, "E117.filletArc", {"start": v(-30.68, -11.18) * mm, "mid": v(-30.54, -11.12) * mm, "end": v(-30.48, -10.97) * mm});
            skPoint(sketch, "E118.visualSharp", {"position": v(-36.17, -11.18) * mm});
            skArc(sketch, "E118.filletArc", {"start": v(-36.17, -10.97) * mm, "mid": v(-36.11, -11.12) * mm, "end": v(-35.97, -11.18) * mm});
            skPoint(sketch, "E119.visualSharp", {"position": v(-30.48, -7.88) * mm});
            skArc(sketch, "E119.filletArc", {"start": v(-30.48, -8.08) * mm, "mid": v(-30.54, -7.94) * mm, "end": v(-30.68, -7.88) * mm});
            skPoint(sketch, "E120.visualSharp", {"position": v(-21.08, -7.88) * mm});
            skArc(sketch, "E120.filletArc", {"start": v(-20.88, -7.88) * mm, "mid": v(-21.02, -7.94) * mm, "end": v(-21.08, -8.08) * mm});
            skPoint(sketch, "E121.visualSharp", {"position": v(-21.08, -11.18) * mm});
            skArc(sketch, "E121.filletArc", {"start": v(-21.08, -10.97) * mm, "mid": v(-21.02, -11.12) * mm, "end": v(-20.88, -11.18) * mm});
            skPoint(sketch, "E122.visualSharp", {"position": v(-15.4, -11.18) * mm});
            skArc(sketch, "E122.filletArc", {"start": v(-15.6, -11.18) * mm, "mid": v(-15.45, -11.12) * mm, "end": v(-15.4, -10.97) * mm});
            skPoint(sketch, "E123.visualSharp", {"position": v(-15.4, -7.88) * mm});
            skArc(sketch, "E123.filletArc", {"start": v(-15.4, -8.08) * mm, "mid": v(-15.45, -7.94) * mm, "end": v(-15.6, -7.88) * mm});
            skPoint(sketch, "E124.visualSharp", {"position": v(-10.67, -7.87) * mm});
            skArc(sketch, "E124.filletArc", {"start": v(-10.46, -7.87) * mm, "mid": v(-10.6, -7.93) * mm, "end": v(-10.67, -8.08) * mm});
            skPoint(sketch, "E125.visualSharp", {"position": v(-10.67, -11.17) * mm});
            skArc(sketch, "E125.filletArc", {"start": v(-10.67, -10.97) * mm, "mid": v(-10.6, -11.11) * mm, "end": v(-10.46, -11.17) * mm});
            skPoint(sketch, "E126.visualSharp", {"position": v(-4.98, -11.17) * mm});
            skArc(sketch, "E126.filletArc", {"start": v(-5.18, -11.17) * mm, "mid": v(-5.04, -11.11) * mm, "end": v(-4.98, -10.97) * mm});
            skPoint(sketch, "E127.visualSharp", {"position": v(-4.98, -7.87) * mm});
            skArc(sketch, "E127.filletArc", {"start": v(-4.98, -8.08) * mm, "mid": v(-5.04, -7.93) * mm, "end": v(-5.18, -7.87) * mm});
            skPoint(sketch, "E128.visualSharp", {"position": v(-5, -2.65) * mm});
            skArc(sketch, "E128.filletArc", {"start": v(-5.2, -2.65) * mm, "mid": v(-5.06, -2.59) * mm, "end": v(-5, -2.44) * mm});
            skPoint(sketch, "E129.visualSharp", {"position": v(-5, 0.65) * mm});
            skArc(sketch, "E129.filletArc", {"start": v(-5, 0.44) * mm, "mid": v(-5.06, 0.59) * mm, "end": v(-5.2, 0.65) * mm});
            skPoint(sketch, "E130.visualSharp", {"position": v(-10.7, 0.65) * mm});
            skArc(sketch, "E130.filletArc", {"start": v(-10.5, 0.65) * mm, "mid": v(-10.63, 0.59) * mm, "end": v(-10.7, 0.44) * mm});
            skPoint(sketch, "E131.visualSharp", {"position": v(-10.7, -2.65) * mm});
            skArc(sketch, "E131.filletArc", {"start": v(-10.7, -2.44) * mm, "mid": v(-10.63, -2.59) * mm, "end": v(-10.5, -2.65) * mm});
            skPoint(sketch, "E132.visualSharp", {"position": v(-10.67, 3.56) * mm});
            skArc(sketch, "E132.filletArc", {"start": v(-10.67, 3.76) * mm, "mid": v(-10.6, 3.62) * mm, "end": v(-10.46, 3.56) * mm});
            skPoint(sketch, "E133.visualSharp", {"position": v(-10.67, 6.85) * mm});
            skArc(sketch, "E133.filletArc", {"start": v(-10.46, 6.85) * mm, "mid": v(-10.6, 6.8) * mm, "end": v(-10.67, 6.65) * mm});
            skPoint(sketch, "E134.visualSharp", {"position": v(-4.98, 6.85) * mm});
            skArc(sketch, "E134.filletArc", {"start": v(-4.98, 6.65) * mm, "mid": v(-5.04, 6.8) * mm, "end": v(-5.18, 6.85) * mm});
            skPoint(sketch, "E135.visualSharp", {"position": v(-4.98, 3.56) * mm});
            skArc(sketch, "E135.filletArc", {"start": v(-5.18, 3.56) * mm, "mid": v(-5.04, 3.62) * mm, "end": v(-4.98, 3.76) * mm});
            skPoint(sketch, "E136.visualSharp", {"position": v(-4.95, 9.76) * mm});
            skArc(sketch, "E136.filletArc", {"start": v(-5.16, 9.76) * mm, "mid": v(-5.01, 9.82) * mm, "end": v(-4.95, 9.96) * mm});
            skPoint(sketch, "E137.visualSharp", {"position": v(-4.95, 13.06) * mm});
            skArc(sketch, "E137.filletArc", {"start": v(-4.95, 12.85) * mm, "mid": v(-5.01, 13) * mm, "end": v(-5.16, 13.06) * mm});
            skPoint(sketch, "E138.visualSharp", {"position": v(-10.64, 13.06) * mm});
            skArc(sketch, "E138.filletArc", {"start": v(-10.44, 13.06) * mm, "mid": v(-10.58, 13) * mm, "end": v(-10.64, 12.85) * mm});
            skPoint(sketch, "E139.visualSharp", {"position": v(-10.64, 9.76) * mm});
            skArc(sketch, "E139.filletArc", {"start": v(-10.64, 9.96) * mm, "mid": v(-10.58, 9.82) * mm, "end": v(-10.44, 9.76) * mm});
            skLineSegment(sketch, "E140.bottom", {"start": v(-33.37, 12.63) * mm, "end": v(-23.53, 12.63) * mm});
            skLineSegment(sketch, "E140.top", {"start": v(-33.37, -1.92) * mm, "end": v(-18.21, -1.92) * mm});
            skLineSegment(sketch, "E140.left", {"start": v(-35.4, 10.6) * mm, "end": v(-35.4, 0.11) * mm});
            skLineSegment(sketch, "E140.right", {"start": v(-16.18, 10.6) * mm, "end": v(-16.18, 0.11) * mm});
            skPoint(sketch, "E141.visualSharp", {"position": v(-35.4, 12.63) * mm});
            skArc(sketch, "E141.filletArc", {"start": v(-33.37, 12.63) * mm, "mid": v(-34.8, 12.04) * mm, "end": v(-35.4, 10.6) * mm});
            skPoint(sketch, "E142.visualSharp", {"position": v(-16.18, 12.63) * mm});
            skPoint(sketch, "E143.visualSharp", {"position": v(-16.18, 10.6) * mm});
            skArc(sketch, "E143.filletArc", {"start": v(-16.18, 10.6) * mm, "mid": v(-16.77, 12.04) * mm, "end": v(-18.21, 12.63) * mm});
            skLineSegment(sketch, "E144", {"start": v(-23.53, 12.63) * mm, "end": v(-18.21, 12.63) * mm});
            skPoint(sketch, "E145.visualSharp", {"position": v(-35.4, -1.92) * mm});
            skArc(sketch, "E145.filletArc", {"start": v(-35.4, 0.11) * mm, "mid": v(-34.8, -1.32) * mm, "end": v(-33.37, -1.92) * mm});
            skPoint(sketch, "E146.visualSharp", {"position": v(-16.18, -1.92) * mm});
            skArc(sketch, "E146.filletArc", {"start": v(-18.21, -1.92) * mm, "mid": v(-16.77, -1.32) * mm, "end": v(-16.18, 0.11) * mm});
            skLineSegment(sketch, "E147.bottom", {"start": v(-46.26, -37.05) * mm, "end": v(-43.25, -37.05) * mm});
            skLineSegment(sketch, "E147.top", {"start": v(-46.26, -39.51) * mm, "end": v(-43.25, -39.51) * mm});
            skLineSegment(sketch, "E147.left", {"start": v(-46.46, -37.26) * mm, "end": v(-46.46, -39.31) * mm});
            skLineSegment(sketch, "E147.right", {"start": v(-43.05, -37.26) * mm, "end": v(-43.05, -39.31) * mm});
            skLineSegment(sketch, "E148.1.0.0", {"start": v(-46.23, -41.17) * mm, "end": v(-43.22, -41.17) * mm});
            skLineSegment(sketch, "E148.1.0.1", {"start": v(-46.43, -41.38) * mm, "end": v(-46.43, -43.36) * mm});
            skLineSegment(sketch, "E148.1.0.2", {"start": v(-43.02, -41.38) * mm, "end": v(-43.02, -43.36) * mm});
            skLineSegment(sketch, "E148.1.0.3", {"start": v(-46.23, -43.57) * mm, "end": v(-43.22, -43.57) * mm});
            skLineSegment(sketch, "E148.2.0.0", {"start": v(-46.2, -45.23) * mm, "end": v(-43.2, -45.23) * mm});
            skLineSegment(sketch, "E148.2.0.1", {"start": v(-46.4, -45.43) * mm, "end": v(-46.4, -47.42) * mm});
            skLineSegment(sketch, "E148.2.0.2", {"start": v(-43, -45.43) * mm, "end": v(-43, -47.42) * mm});
            skLineSegment(sketch, "E148.2.0.3", {"start": v(-46.2, -47.62) * mm, "end": v(-43.2, -47.62) * mm});
            skLineSegment(sketch, "E149.1.0.0", {"start": v(-4.72, -36.75) * mm, "end": v(-4.72, -39.14) * mm});
            skLineSegment(sketch, "E149.1.0.1", {"start": v(-8.13, -36.75) * mm, "end": v(-4.72, -36.75) * mm});
            skLineSegment(sketch, "E149.1.0.2", {"start": v(-8.13, -36.75) * mm, "end": v(-8.13, -39.14) * mm});
            skLineSegment(sketch, "E149.1.0.3", {"start": v(-8.13, -39.14) * mm, "end": v(-4.72, -39.14) * mm});
            skLineSegment(sketch, "E150.1.0.0", {"start": v(-8.1, -40.81) * mm, "end": v(-8.1, -43.2) * mm});
            skLineSegment(sketch, "E150.1.0.1", {"start": v(-8.1, -40.81) * mm, "end": v(-4.7, -40.81) * mm});
            skLineSegment(sketch, "E150.1.0.2", {"start": v(-4.7, -40.81) * mm, "end": v(-4.7, -43.2) * mm});
            skLineSegment(sketch, "E150.1.0.3", {"start": v(-8.1, -43.2) * mm, "end": v(-4.7, -43.2) * mm});
            skLineSegment(sketch, "E150.2.0.0", {"start": v(-8.07, -44.87) * mm, "end": v(-8.07, -47.27) * mm});
            skLineSegment(sketch, "E150.2.0.1", {"start": v(-8.07, -44.87) * mm, "end": v(-4.66, -44.87) * mm});
            skLineSegment(sketch, "E150.2.0.2", {"start": v(-4.66, -44.87) * mm, "end": v(-4.66, -47.27) * mm});
            skLineSegment(sketch, "E150.2.0.3", {"start": v(-8.07, -47.27) * mm, "end": v(-4.66, -47.27) * mm});
            skLineSegment(sketch, "E151.bottom", {"start": v(-40.66, -37.12) * mm, "end": v(-38.45, -37.12) * mm});
            skLineSegment(sketch, "E151.top", {"start": v(-40.66, -39.43) * mm, "end": v(-38.45, -39.43) * mm});
            skLineSegment(sketch, "E151.left", {"start": v(-40.86, -37.32) * mm, "end": v(-40.86, -39.23) * mm});
            skLineSegment(sketch, "E151.right", {"start": v(-38.25, -37.32) * mm, "end": v(-38.25, -39.23) * mm});
            skLineSegment(sketch, "E152.1.0.0", {"start": v(-36.02, -37.03) * mm, "end": v(-33.81, -37.03) * mm});
            skLineSegment(sketch, "E152.1.0.1", {"start": v(-36.22, -37.24) * mm, "end": v(-36.22, -39.14) * mm});
            skLineSegment(sketch, "E152.1.0.2", {"start": v(-36.02, -39.35) * mm, "end": v(-33.81, -39.35) * mm});
            skLineSegment(sketch, "E152.1.0.3", {"start": v(-33.61, -37.24) * mm, "end": v(-33.61, -39.14) * mm});
            skLineSegment(sketch, "E152.2.0.0", {"start": v(-31.38, -36.95) * mm, "end": v(-29.18, -36.95) * mm});
            skLineSegment(sketch, "E152.2.0.1", {"start": v(-31.58, -37.15) * mm, "end": v(-31.58, -39.06) * mm});
            skLineSegment(sketch, "E152.2.0.2", {"start": v(-31.38, -39.26) * mm, "end": v(-29.18, -39.26) * mm});
            skLineSegment(sketch, "E152.2.0.3", {"start": v(-28.97, -37.15) * mm, "end": v(-28.97, -39.06) * mm});
            skLineSegment(sketch, "E152.3.0.0", {"start": v(-26.74, -36.86) * mm, "end": v(-24.33, -36.86) * mm});
            skLineSegment(sketch, "E152.3.0.1", {"start": v(-26.94, -37.06) * mm, "end": v(-26.94, -39.17) * mm});
            skLineSegment(sketch, "E152.3.0.2", {"start": v(-26.94, -39.17) * mm, "end": v(-24.33, -39.17) * mm});
            skLineSegment(sketch, "E152.3.0.3", {"start": v(-24.33, -36.86) * mm, "end": v(-24.33, -39.17) * mm});
            skLineSegment(sketch, "E152.4.0.0", {"start": v(-22.3, -36.77) * mm, "end": v(-19.7, -36.77) * mm});
            skLineSegment(sketch, "E152.4.0.1", {"start": v(-22.3, -36.77) * mm, "end": v(-22.3, -39.09) * mm});
            skLineSegment(sketch, "E152.4.0.2", {"start": v(-22.3, -39.09) * mm, "end": v(-19.7, -39.09) * mm});
            skLineSegment(sketch, "E152.4.0.3", {"start": v(-19.7, -36.77) * mm, "end": v(-19.7, -39.09) * mm});
            skLineSegment(sketch, "E152.5.0.0", {"start": v(-17.67, -36.69) * mm, "end": v(-15.06, -36.69) * mm});
            skLineSegment(sketch, "E152.5.0.1", {"start": v(-17.67, -36.69) * mm, "end": v(-17.67, -39) * mm});
            skLineSegment(sketch, "E152.5.0.2", {"start": v(-17.67, -39) * mm, "end": v(-15.06, -39) * mm});
            skLineSegment(sketch, "E152.5.0.3", {"start": v(-15.06, -36.69) * mm, "end": v(-15.06, -39) * mm});
            skLineSegment(sketch, "E152.6.0.0", {"start": v(-13.03, -36.6) * mm, "end": v(-10.42, -36.6) * mm});
            skLineSegment(sketch, "E152.6.0.1", {"start": v(-13.03, -36.6) * mm, "end": v(-13.03, -38.91) * mm});
            skLineSegment(sketch, "E152.6.0.2", {"start": v(-13.03, -38.91) * mm, "end": v(-10.42, -38.91) * mm});
            skLineSegment(sketch, "E152.6.0.3", {"start": v(-10.42, -36.6) * mm, "end": v(-10.42, -38.91) * mm});
            skLineSegment(sketch, "E153.1.0.0", {"start": v(-40.8, -41.48) * mm, "end": v(-40.8, -43.38) * mm});
            skLineSegment(sketch, "E153.1.0.1", {"start": v(-40.59, -41.27) * mm, "end": v(-38.39, -41.27) * mm});
            skLineSegment(sketch, "E153.1.0.2", {"start": v(-38.18, -41.48) * mm, "end": v(-38.18, -43.38) * mm});
            skLineSegment(sketch, "E153.1.0.3", {"start": v(-40.59, -43.59) * mm, "end": v(-38.39, -43.59) * mm});
            skLineSegment(sketch, "E153.1.0.4", {"start": v(-36.15, -41.39) * mm, "end": v(-36.15, -43.3) * mm});
            skLineSegment(sketch, "E153.1.0.5", {"start": v(-35.95, -41.19) * mm, "end": v(-33.75, -41.19) * mm});
            skLineSegment(sketch, "E153.1.0.6", {"start": v(-33.54, -41.39) * mm, "end": v(-33.54, -43.3) * mm});
            skLineSegment(sketch, "E153.1.0.7", {"start": v(-35.95, -43.5) * mm, "end": v(-33.75, -43.5) * mm});
            skLineSegment(sketch, "E153.1.0.8", {"start": v(-31.51, -41.3) * mm, "end": v(-31.51, -43.2) * mm});
            skLineSegment(sketch, "E153.1.0.9", {"start": v(-31.31, -41.1) * mm, "end": v(-29.1, -41.1) * mm});
            skLineSegment(sketch, "E153.1.0.10", {"start": v(-28.9, -41.3) * mm, "end": v(-28.9, -43.2) * mm});
            skLineSegment(sketch, "E153.1.0.11", {"start": v(-31.31, -43.41) * mm, "end": v(-29.1, -43.41) * mm});
            skLineSegment(sketch, "E153.1.0.12", {"start": v(-26.88, -41.01) * mm, "end": v(-26.88, -43.33) * mm});
            skLineSegment(sketch, "E153.1.0.13", {"start": v(-26.88, -41.01) * mm, "end": v(-24.27, -41.01) * mm});
            skLineSegment(sketch, "E153.1.0.14", {"start": v(-24.27, -41.01) * mm, "end": v(-24.27, -43.33) * mm});
            skLineSegment(sketch, "E153.1.0.15", {"start": v(-26.88, -43.33) * mm, "end": v(-24.27, -43.33) * mm});
            skLineSegment(sketch, "E153.1.0.16", {"start": v(-22.24, -40.92) * mm, "end": v(-22.24, -43.24) * mm});
            skLineSegment(sketch, "E153.1.0.17", {"start": v(-22.24, -40.92) * mm, "end": v(-19.63, -40.92) * mm});
            skLineSegment(sketch, "E153.1.0.18", {"start": v(-19.63, -40.92) * mm, "end": v(-19.63, -43.24) * mm});
            skLineSegment(sketch, "E153.1.0.19", {"start": v(-22.24, -43.24) * mm, "end": v(-19.63, -43.24) * mm});
            skLineSegment(sketch, "E153.1.0.20", {"start": v(-17.6, -40.84) * mm, "end": v(-17.6, -43.15) * mm});
            skLineSegment(sketch, "E153.1.0.21", {"start": v(-17.6, -40.84) * mm, "end": v(-14.99, -40.84) * mm});
            skLineSegment(sketch, "E153.1.0.22", {"start": v(-14.99, -40.84) * mm, "end": v(-14.99, -43.15) * mm});
            skLineSegment(sketch, "E153.1.0.23", {"start": v(-17.6, -43.15) * mm, "end": v(-14.99, -43.15) * mm});
            skLineSegment(sketch, "E153.1.0.24", {"start": v(-12.96, -40.75) * mm, "end": v(-12.96, -43.06) * mm});
            skLineSegment(sketch, "E153.1.0.25", {"start": v(-12.96, -40.75) * mm, "end": v(-10.35, -40.75) * mm});
            skLineSegment(sketch, "E153.1.0.26", {"start": v(-10.35, -40.75) * mm, "end": v(-10.35, -43.06) * mm});
            skLineSegment(sketch, "E153.1.0.27", {"start": v(-12.96, -43.06) * mm, "end": v(-10.35, -43.06) * mm});
            skLineSegment(sketch, "E153.2.0.0", {"start": v(-40.73, -45.63) * mm, "end": v(-40.73, -47.54) * mm});
            skLineSegment(sketch, "E153.2.0.1", {"start": v(-40.52, -45.42) * mm, "end": v(-38.32, -45.42) * mm});
            skLineSegment(sketch, "E153.2.0.2", {"start": v(-38.12, -45.63) * mm, "end": v(-38.12, -47.54) * mm});
            skLineSegment(sketch, "E153.2.0.3", {"start": v(-40.52, -47.74) * mm, "end": v(-38.32, -47.74) * mm});
            skLineSegment(sketch, "E153.2.0.4", {"start": v(-36.09, -45.54) * mm, "end": v(-36.09, -47.45) * mm});
            skLineSegment(sketch, "E153.2.0.5", {"start": v(-35.88, -45.34) * mm, "end": v(-33.68, -45.34) * mm});
            skLineSegment(sketch, "E153.2.0.6", {"start": v(-33.48, -45.54) * mm, "end": v(-33.48, -47.45) * mm});
            skLineSegment(sketch, "E153.2.0.7", {"start": v(-35.88, -47.65) * mm, "end": v(-33.68, -47.65) * mm});
            skLineSegment(sketch, "E153.2.0.8", {"start": v(-31.45, -45.45) * mm, "end": v(-31.45, -47.36) * mm});
            skLineSegment(sketch, "E153.2.0.9", {"start": v(-31.24, -45.25) * mm, "end": v(-29.04, -45.25) * mm});
            skLineSegment(sketch, "E153.2.0.10", {"start": v(-28.84, -45.45) * mm, "end": v(-28.84, -47.36) * mm});
            skLineSegment(sketch, "E153.2.0.11", {"start": v(-31.24, -47.56) * mm, "end": v(-29.04, -47.56) * mm});
            skLineSegment(sketch, "E153.2.0.12", {"start": v(-26.8, -45.16) * mm, "end": v(-26.8, -47.48) * mm});
            skLineSegment(sketch, "E153.2.0.13", {"start": v(-26.8, -45.16) * mm, "end": v(-24.2, -45.16) * mm});
            skLineSegment(sketch, "E153.2.0.14", {"start": v(-24.2, -45.16) * mm, "end": v(-24.2, -47.48) * mm});
            skLineSegment(sketch, "E153.2.0.15", {"start": v(-26.8, -47.48) * mm, "end": v(-24.2, -47.48) * mm});
            skLineSegment(sketch, "E153.2.0.16", {"start": v(-22.17, -45.08) * mm, "end": v(-22.17, -47.4) * mm});
            skLineSegment(sketch, "E153.2.0.17", {"start": v(-22.17, -45.08) * mm, "end": v(-19.56, -45.08) * mm});
            skLineSegment(sketch, "E153.2.0.18", {"start": v(-19.56, -45.08) * mm, "end": v(-19.56, -47.4) * mm});
            skLineSegment(sketch, "E153.2.0.19", {"start": v(-22.17, -47.4) * mm, "end": v(-19.56, -47.4) * mm});
            skLineSegment(sketch, "E153.2.0.20", {"start": v(-17.53, -44.99) * mm, "end": v(-17.53, -47.3) * mm});
            skLineSegment(sketch, "E153.2.0.21", {"start": v(-17.53, -44.99) * mm, "end": v(-14.92, -44.99) * mm});
            skLineSegment(sketch, "E153.2.0.22", {"start": v(-14.92, -44.99) * mm, "end": v(-14.92, -47.3) * mm});
            skLineSegment(sketch, "E153.2.0.23", {"start": v(-17.53, -47.3) * mm, "end": v(-14.92, -47.3) * mm});
            skLineSegment(sketch, "E153.2.0.24", {"start": v(-12.9, -44.9) * mm, "end": v(-12.9, -47.22) * mm});
            skLineSegment(sketch, "E153.2.0.25", {"start": v(-12.9, -44.9) * mm, "end": v(-10.28, -44.9) * mm});
            skLineSegment(sketch, "E153.2.0.26", {"start": v(-10.28, -44.9) * mm, "end": v(-10.28, -47.22) * mm});
            skLineSegment(sketch, "E153.2.0.27", {"start": v(-12.9, -47.22) * mm, "end": v(-10.28, -47.22) * mm});
            skLineSegment(sketch, "E154.1.0.0", {"start": v(-40.46, -49.4) * mm, "end": v(-38.26, -49.4) * mm});
            skLineSegment(sketch, "E154.1.0.1", {"start": v(-40.67, -49.6) * mm, "end": v(-40.67, -51.51) * mm});
            skLineSegment(sketch, "E154.1.0.2", {"start": v(-40.46, -51.72) * mm, "end": v(-38.26, -51.72) * mm});
            skLineSegment(sketch, "E154.1.0.3", {"start": v(-38.06, -49.6) * mm, "end": v(-38.06, -51.51) * mm});
            skLineSegment(sketch, "E154.1.0.4", {"start": v(-36.03, -49.52) * mm, "end": v(-36.03, -51.43) * mm});
            skLineSegment(sketch, "E154.1.0.5", {"start": v(-35.82, -49.32) * mm, "end": v(-33.62, -49.32) * mm});
            skLineSegment(sketch, "E154.1.0.6", {"start": v(-33.42, -49.52) * mm, "end": v(-33.42, -51.43) * mm});
            skLineSegment(sketch, "E154.1.0.7", {"start": v(-35.82, -51.63) * mm, "end": v(-33.62, -51.63) * mm});
            skLineSegment(sketch, "E154.1.0.8", {"start": v(-31.39, -49.43) * mm, "end": v(-31.39, -51.34) * mm});
            skLineSegment(sketch, "E154.1.0.9", {"start": v(-31.18, -49.23) * mm, "end": v(-28.98, -49.23) * mm});
            skLineSegment(sketch, "E154.1.0.10", {"start": v(-28.78, -49.43) * mm, "end": v(-28.78, -51.34) * mm});
            skLineSegment(sketch, "E154.1.0.11", {"start": v(-31.18, -51.54) * mm, "end": v(-28.98, -51.54) * mm});
            skLineSegment(sketch, "E154.1.0.12", {"start": v(-26.75, -49.14) * mm, "end": v(-26.75, -51.46) * mm});
            skLineSegment(sketch, "E154.1.0.13", {"start": v(-26.75, -49.14) * mm, "end": v(-24.14, -49.14) * mm});
            skLineSegment(sketch, "E154.1.0.14", {"start": v(-24.14, -49.14) * mm, "end": v(-24.14, -51.46) * mm});
            skLineSegment(sketch, "E154.1.0.15", {"start": v(-26.75, -51.46) * mm, "end": v(-24.14, -51.46) * mm});
            skLineSegment(sketch, "E154.1.0.16", {"start": v(-22.11, -49.06) * mm, "end": v(-22.11, -51.37) * mm});
            skLineSegment(sketch, "E154.1.0.17", {"start": v(-22.11, -49.06) * mm, "end": v(-19.5, -49.06) * mm});
            skLineSegment(sketch, "E154.1.0.18", {"start": v(-19.5, -49.06) * mm, "end": v(-19.5, -51.37) * mm});
            skLineSegment(sketch, "E154.1.0.19", {"start": v(-22.11, -51.37) * mm, "end": v(-19.5, -51.37) * mm});
            skLineSegment(sketch, "E155.bottom", {"start": v(-17.19, -49.25) * mm, "end": v(-10.11, -49.25) * mm});
            skLineSegment(sketch, "E155.top", {"start": v(-17.19, -51.43) * mm, "end": v(-10.11, -51.43) * mm});
            skLineSegment(sketch, "E155.left", {"start": v(-17.19, -49.25) * mm, "end": v(-17.19, -51.43) * mm});
            skLineSegment(sketch, "E155.right", {"start": v(-10.11, -49.25) * mm, "end": v(-10.11, -51.43) * mm});
            skPoint(sketch, "E156.visualSharp", {"position": v(-46.46, -37.05) * mm});
            skArc(sketch, "E156.filletArc", {"start": v(-46.26, -37.05) * mm, "mid": v(-46.4, -37.11) * mm, "end": v(-46.46, -37.26) * mm});
            skPoint(sketch, "E157.visualSharp", {"position": v(-43.05, -39.51) * mm});
            skArc(sketch, "E157.filletArc", {"start": v(-43.25, -39.51) * mm, "mid": v(-43.11, -39.45) * mm, "end": v(-43.05, -39.31) * mm});
            skPoint(sketch, "E158.visualSharp", {"position": v(-43.05, -37.05) * mm});
            skArc(sketch, "E158.filletArc", {"start": v(-43.05, -37.26) * mm, "mid": v(-43.11, -37.11) * mm, "end": v(-43.25, -37.05) * mm});
            skPoint(sketch, "E159.visualSharp", {"position": v(-46.46, -39.51) * mm});
            skArc(sketch, "E159.filletArc", {"start": v(-46.46, -39.31) * mm, "mid": v(-46.4, -39.45) * mm, "end": v(-46.26, -39.51) * mm});
            skPoint(sketch, "E160.visualSharp", {"position": v(-40.86, -37.12) * mm});
            skArc(sketch, "E160.filletArc", {"start": v(-40.66, -37.12) * mm, "mid": v(-40.8, -37.18) * mm, "end": v(-40.86, -37.32) * mm});
            skPoint(sketch, "E161.visualSharp", {"position": v(-46.43, -41.17) * mm});
            skArc(sketch, "E161.filletArc", {"start": v(-46.23, -41.17) * mm, "mid": v(-46.37, -41.23) * mm, "end": v(-46.43, -41.38) * mm});
            skPoint(sketch, "E162.visualSharp", {"position": v(-46.43, -43.57) * mm});
            skArc(sketch, "E162.filletArc", {"start": v(-46.43, -43.36) * mm, "mid": v(-46.37, -43.5) * mm, "end": v(-46.23, -43.57) * mm});
            skPoint(sketch, "E163.visualSharp", {"position": v(-46.4, -45.23) * mm});
            skArc(sketch, "E163.filletArc", {"start": v(-46.2, -45.23) * mm, "mid": v(-46.34, -45.29) * mm, "end": v(-46.4, -45.43) * mm});
            skPoint(sketch, "E164.visualSharp", {"position": v(-46.4, -47.62) * mm});
            skArc(sketch, "E164.filletArc", {"start": v(-46.4, -47.42) * mm, "mid": v(-46.34, -47.56) * mm, "end": v(-46.2, -47.62) * mm});
            skPoint(sketch, "E165.visualSharp", {"position": v(-43, -47.62) * mm});
            skArc(sketch, "E165.filletArc", {"start": v(-43.2, -47.62) * mm, "mid": v(-43.05, -47.56) * mm, "end": v(-43, -47.42) * mm});
            skPoint(sketch, "E166.visualSharp", {"position": v(-43, -45.23) * mm});
            skArc(sketch, "E166.filletArc", {"start": v(-43, -45.43) * mm, "mid": v(-43.05, -45.29) * mm, "end": v(-43.2, -45.23) * mm});
            skPoint(sketch, "E167.visualSharp", {"position": v(-43.02, -43.57) * mm});
            skArc(sketch, "E167.filletArc", {"start": v(-43.22, -43.57) * mm, "mid": v(-43.08, -43.5) * mm, "end": v(-43.02, -43.36) * mm});
            skPoint(sketch, "E168.visualSharp", {"position": v(-43.02, -41.17) * mm});
            skArc(sketch, "E168.filletArc", {"start": v(-43.02, -41.38) * mm, "mid": v(-43.08, -41.23) * mm, "end": v(-43.22, -41.17) * mm});
            skPoint(sketch, "E169.visualSharp", {"position": v(-40.86, -39.43) * mm});
            skArc(sketch, "E169.filletArc", {"start": v(-40.86, -39.23) * mm, "mid": v(-40.8, -39.37) * mm, "end": v(-40.66, -39.43) * mm});
            skPoint(sketch, "E170.visualSharp", {"position": v(-40.8, -41.27) * mm});
            skArc(sketch, "E170.filletArc", {"start": v(-40.59, -41.27) * mm, "mid": v(-40.73, -41.33) * mm, "end": v(-40.8, -41.48) * mm});
            skPoint(sketch, "E171.visualSharp", {"position": v(-40.8, -43.59) * mm});
            skArc(sketch, "E171.filletArc", {"start": v(-40.8, -43.38) * mm, "mid": v(-40.73, -43.53) * mm, "end": v(-40.59, -43.59) * mm});
            skPoint(sketch, "E172.visualSharp", {"position": v(-40.73, -45.42) * mm});
            skArc(sketch, "E172.filletArc", {"start": v(-40.52, -45.42) * mm, "mid": v(-40.67, -45.48) * mm, "end": v(-40.73, -45.63) * mm});
            skPoint(sketch, "E173.visualSharp", {"position": v(-40.73, -47.74) * mm});
            skArc(sketch, "E173.filletArc", {"start": v(-40.73, -47.54) * mm, "mid": v(-40.67, -47.68) * mm, "end": v(-40.52, -47.74) * mm});
            skPoint(sketch, "E174.visualSharp", {"position": v(-40.67, -49.4) * mm});
            skArc(sketch, "E174.filletArc", {"start": v(-40.46, -49.4) * mm, "mid": v(-40.6, -49.46) * mm, "end": v(-40.67, -49.6) * mm});
            skPoint(sketch, "E175.visualSharp", {"position": v(-40.67, -51.72) * mm});
            skArc(sketch, "E175.filletArc", {"start": v(-40.67, -51.51) * mm, "mid": v(-40.6, -51.66) * mm, "end": v(-40.46, -51.72) * mm});
            skPoint(sketch, "E176.visualSharp", {"position": v(-38.06, -51.72) * mm});
            skArc(sketch, "E176.filletArc", {"start": v(-38.26, -51.72) * mm, "mid": v(-38.12, -51.66) * mm, "end": v(-38.06, -51.51) * mm});
            skPoint(sketch, "E177.visualSharp", {"position": v(-38.06, -49.4) * mm});
            skArc(sketch, "E177.filletArc", {"start": v(-38.06, -49.6) * mm, "mid": v(-38.12, -49.46) * mm, "end": v(-38.26, -49.4) * mm});
            skPoint(sketch, "E178.visualSharp", {"position": v(-38.12, -47.74) * mm});
            skArc(sketch, "E178.filletArc", {"start": v(-38.32, -47.74) * mm, "mid": v(-38.18, -47.68) * mm, "end": v(-38.12, -47.54) * mm});
            skPoint(sketch, "E179.visualSharp", {"position": v(-38.12, -45.42) * mm});
            skArc(sketch, "E179.filletArc", {"start": v(-38.12, -45.63) * mm, "mid": v(-38.18, -45.48) * mm, "end": v(-38.32, -45.42) * mm});
            skPoint(sketch, "E180.visualSharp", {"position": v(-38.18, -43.59) * mm});
            skArc(sketch, "E180.filletArc", {"start": v(-38.39, -43.59) * mm, "mid": v(-38.24, -43.53) * mm, "end": v(-38.18, -43.38) * mm});
            skPoint(sketch, "E181.visualSharp", {"position": v(-38.18, -41.27) * mm});
            skArc(sketch, "E181.filletArc", {"start": v(-38.18, -41.48) * mm, "mid": v(-38.24, -41.33) * mm, "end": v(-38.39, -41.27) * mm});
            skPoint(sketch, "E182.visualSharp", {"position": v(-38.25, -39.43) * mm});
            skArc(sketch, "E182.filletArc", {"start": v(-38.45, -39.43) * mm, "mid": v(-38.3, -39.37) * mm, "end": v(-38.25, -39.23) * mm});
            skPoint(sketch, "E183.visualSharp", {"position": v(-38.25, -37.12) * mm});
            skArc(sketch, "E183.filletArc", {"start": v(-38.25, -37.32) * mm, "mid": v(-38.3, -37.18) * mm, "end": v(-38.45, -37.12) * mm});
            skPoint(sketch, "E184.visualSharp", {"position": v(-36.22, -37.03) * mm});
            skArc(sketch, "E184.filletArc", {"start": v(-36.02, -37.03) * mm, "mid": v(-36.16, -37.1) * mm, "end": v(-36.22, -37.24) * mm});
            skPoint(sketch, "E185.visualSharp", {"position": v(-36.22, -39.35) * mm});
            skArc(sketch, "E185.filletArc", {"start": v(-36.22, -39.14) * mm, "mid": v(-36.16, -39.29) * mm, "end": v(-36.02, -39.35) * mm});
            skPoint(sketch, "E186.visualSharp", {"position": v(-36.15, -41.19) * mm});
            skArc(sketch, "E186.filletArc", {"start": v(-35.95, -41.19) * mm, "mid": v(-36.1, -41.24) * mm, "end": v(-36.15, -41.39) * mm});
            skPoint(sketch, "E187.visualSharp", {"position": v(-36.15, -43.5) * mm});
            skArc(sketch, "E187.filletArc", {"start": v(-36.15, -43.3) * mm, "mid": v(-36.1, -43.44) * mm, "end": v(-35.95, -43.5) * mm});
            skPoint(sketch, "E188.visualSharp", {"position": v(-36.09, -45.34) * mm});
            skArc(sketch, "E188.filletArc", {"start": v(-35.88, -45.34) * mm, "mid": v(-36.03, -45.4) * mm, "end": v(-36.09, -45.54) * mm});
            skPoint(sketch, "E189.visualSharp", {"position": v(-36.09, -47.65) * mm});
            skArc(sketch, "E189.filletArc", {"start": v(-36.09, -47.45) * mm, "mid": v(-36.03, -47.6) * mm, "end": v(-35.88, -47.65) * mm});
            skPoint(sketch, "E190.visualSharp", {"position": v(-36.03, -49.32) * mm});
            skArc(sketch, "E190.filletArc", {"start": v(-35.82, -49.32) * mm, "mid": v(-35.97, -49.38) * mm, "end": v(-36.03, -49.52) * mm});
            skPoint(sketch, "E191.visualSharp", {"position": v(-36.03, -51.63) * mm});
            skArc(sketch, "E191.filletArc", {"start": v(-36.03, -51.43) * mm, "mid": v(-35.97, -51.57) * mm, "end": v(-35.82, -51.63) * mm});
            skPoint(sketch, "E192.visualSharp", {"position": v(-33.42, -51.63) * mm});
            skArc(sketch, "E192.filletArc", {"start": v(-33.62, -51.63) * mm, "mid": v(-33.48, -51.57) * mm, "end": v(-33.42, -51.43) * mm});
            skPoint(sketch, "E193.visualSharp", {"position": v(-33.42, -49.32) * mm});
            skArc(sketch, "E193.filletArc", {"start": v(-33.42, -49.52) * mm, "mid": v(-33.48, -49.38) * mm, "end": v(-33.62, -49.32) * mm});
            skPoint(sketch, "E194.visualSharp", {"position": v(-33.48, -47.65) * mm});
            skArc(sketch, "E194.filletArc", {"start": v(-33.68, -47.65) * mm, "mid": v(-33.54, -47.6) * mm, "end": v(-33.48, -47.45) * mm});
            skPoint(sketch, "E195.visualSharp", {"position": v(-33.48, -45.34) * mm});
            skArc(sketch, "E195.filletArc", {"start": v(-33.48, -45.54) * mm, "mid": v(-33.54, -45.4) * mm, "end": v(-33.68, -45.34) * mm});
            skPoint(sketch, "E196.visualSharp", {"position": v(-33.54, -43.5) * mm});
            skArc(sketch, "E196.filletArc", {"start": v(-33.75, -43.5) * mm, "mid": v(-33.6, -43.44) * mm, "end": v(-33.54, -43.3) * mm});
            skPoint(sketch, "E197.visualSharp", {"position": v(-33.54, -41.19) * mm});
            skArc(sketch, "E197.filletArc", {"start": v(-33.54, -41.39) * mm, "mid": v(-33.6, -41.24) * mm, "end": v(-33.75, -41.19) * mm});
            skPoint(sketch, "E198.visualSharp", {"position": v(-33.61, -39.35) * mm});
            skArc(sketch, "E198.filletArc", {"start": v(-33.81, -39.35) * mm, "mid": v(-33.67, -39.29) * mm, "end": v(-33.61, -39.14) * mm});
            skPoint(sketch, "E199.visualSharp", {"position": v(-33.61, -37.03) * mm});
            skArc(sketch, "E199.filletArc", {"start": v(-33.61, -37.24) * mm, "mid": v(-33.67, -37.1) * mm, "end": v(-33.81, -37.03) * mm});
            skPoint(sketch, "E200.visualSharp", {"position": v(-31.58, -36.95) * mm});
            skArc(sketch, "E200.filletArc", {"start": v(-31.38, -36.95) * mm, "mid": v(-31.52, -37) * mm, "end": v(-31.58, -37.15) * mm});
            skPoint(sketch, "E201.visualSharp", {"position": v(-31.58, -39.26) * mm});
            skArc(sketch, "E201.filletArc", {"start": v(-31.58, -39.06) * mm, "mid": v(-31.52, -39.2) * mm, "end": v(-31.38, -39.26) * mm});
            skPoint(sketch, "E202.visualSharp", {"position": v(-31.51, -41.1) * mm});
            skArc(sketch, "E202.filletArc", {"start": v(-31.31, -41.1) * mm, "mid": v(-31.46, -41.16) * mm, "end": v(-31.51, -41.3) * mm});
            skPoint(sketch, "E203.visualSharp", {"position": v(-31.51, -43.41) * mm});
            skArc(sketch, "E203.filletArc", {"start": v(-31.51, -43.2) * mm, "mid": v(-31.46, -43.35) * mm, "end": v(-31.31, -43.41) * mm});
            skPoint(sketch, "E204.visualSharp", {"position": v(-31.45, -45.25) * mm});
            skArc(sketch, "E204.filletArc", {"start": v(-31.24, -45.25) * mm, "mid": v(-31.39, -45.31) * mm, "end": v(-31.45, -45.45) * mm});
            skPoint(sketch, "E205.visualSharp", {"position": v(-31.45, -47.56) * mm});
            skArc(sketch, "E205.filletArc", {"start": v(-31.45, -47.36) * mm, "mid": v(-31.39, -47.5) * mm, "end": v(-31.24, -47.56) * mm});
            skPoint(sketch, "E206.visualSharp", {"position": v(-31.39, -49.23) * mm});
            skArc(sketch, "E206.filletArc", {"start": v(-31.18, -49.23) * mm, "mid": v(-31.33, -49.29) * mm, "end": v(-31.39, -49.43) * mm});
            skPoint(sketch, "E207.visualSharp", {"position": v(-31.39, -51.54) * mm});
            skArc(sketch, "E207.filletArc", {"start": v(-31.39, -51.34) * mm, "mid": v(-31.33, -51.48) * mm, "end": v(-31.18, -51.54) * mm});
            skPoint(sketch, "E208.visualSharp", {"position": v(-28.78, -51.54) * mm});
            skArc(sketch, "E208.filletArc", {"start": v(-28.98, -51.54) * mm, "mid": v(-28.84, -51.48) * mm, "end": v(-28.78, -51.34) * mm});
            skPoint(sketch, "E209.visualSharp", {"position": v(-28.78, -49.23) * mm});
            skArc(sketch, "E209.filletArc", {"start": v(-28.78, -49.43) * mm, "mid": v(-28.84, -49.29) * mm, "end": v(-28.98, -49.23) * mm});
            skPoint(sketch, "E210.visualSharp", {"position": v(-28.84, -47.56) * mm});
            skArc(sketch, "E210.filletArc", {"start": v(-29.04, -47.56) * mm, "mid": v(-28.9, -47.5) * mm, "end": v(-28.84, -47.36) * mm});
            skPoint(sketch, "E211.visualSharp", {"position": v(-28.84, -45.25) * mm});
            skArc(sketch, "E211.filletArc", {"start": v(-28.84, -45.45) * mm, "mid": v(-28.9, -45.31) * mm, "end": v(-29.04, -45.25) * mm});
            skPoint(sketch, "E212.visualSharp", {"position": v(-28.9, -43.41) * mm});
            skArc(sketch, "E212.filletArc", {"start": v(-29.1, -43.41) * mm, "mid": v(-28.96, -43.35) * mm, "end": v(-28.9, -43.2) * mm});
            skPoint(sketch, "E213.visualSharp", {"position": v(-28.9, -41.1) * mm});
            skArc(sketch, "E213.filletArc", {"start": v(-28.9, -41.3) * mm, "mid": v(-28.96, -41.16) * mm, "end": v(-29.1, -41.1) * mm});
            skPoint(sketch, "E214.visualSharp", {"position": v(-28.97, -39.26) * mm});
            skArc(sketch, "E214.filletArc", {"start": v(-29.18, -39.26) * mm, "mid": v(-29.03, -39.2) * mm, "end": v(-28.97, -39.06) * mm});
            skPoint(sketch, "E215.visualSharp", {"position": v(-28.97, -36.95) * mm});
            skArc(sketch, "E215.filletArc", {"start": v(-28.97, -37.15) * mm, "mid": v(-29.03, -37) * mm, "end": v(-29.18, -36.95) * mm});
            skPoint(sketch, "E216.visualSharp", {"position": v(-26.94, -36.86) * mm});
            skArc(sketch, "E216.filletArc", {"start": v(-26.74, -36.86) * mm, "mid": v(-26.88, -36.92) * mm, "end": v(-26.94, -37.06) * mm});
            skSolve(sketch);
        }
        {
            var Q0;
            Q0=qCreatedBy(makeId("Front.planeOp"),FACE);
            var sketch = newSketch(context, id + "F1", { "sketchPlane" : qUnion([Q0])});
            skLineSegment(sketch, "E217.bottom", {"start": v(-48.06, 55) * mm, "end": v(-2.9, 55) * mm});
            skLineSegment(sketch, "E217.top", {"start": v(-41.7, -56.32) * mm, "end": v(-9.25, -56.32) * mm});
            skLineSegment(sketch, "E217.left", {"start": v(-48.06, 55) * mm, "end": v(-48.06, -49.97) * mm});
            skLineSegment(sketch, "E217.right", {"start": v(-2.9, 55) * mm, "end": v(-2.9, -49.97) * mm});
            skPoint(sketch, "E218.visualSharp", {"position": v(-48.06, -56.32) * mm});
            skArc(sketch, "E218.filletArc", {"start": v(-48.06, -49.97) * mm, "mid": v(-46.2, -54.46) * mm, "end": v(-41.7, -56.32) * mm});
            skPoint(sketch, "E219.visualSharp", {"position": v(-2.9, -56.32) * mm});
            skArc(sketch, "E219.filletArc", {"start": v(-9.25, -56.32) * mm, "mid": v(-4.76, -54.46) * mm, "end": v(-2.9, -49.97) * mm});
            skSolve(sketch);
        }
        {
            var Q0;
            Q0 = qSketchRegion(id + "F0", true);
            extrude(context, id + "F2", {"entities" : qUnion([Q0]), "depth" : 2 * mm});
        }
        {
            var Q0;
            Q0 = qSketchRegion(id + "F1", true);
            extrude(context, id + "F3", {"entities" : qUnion([Q0]), "oppositeDirection" : true, "depth" : 6.38 * mm});
        }
        {
            var Q0;
            Q0=makeQuery(id+"F3.opExtrude","SWEPT_FACE",FACE,{"disambiguationData":[OSD([sQuery(id+"F1.wireOp",EDGE,"E217.bottom")])]});
            var sketch = newSketch(context, id + "F4", { "sketchPlane" : qUnion([Q0])});
            skLineSegment(sketch, "E220.bottom", {"start": v(-42.3, 4.5) * mm, "end": v(-34.5, 4.46) * mm});
            skLineSegment(sketch, "E220.top", {"start": v(-42.3, 3.16) * mm, "end": v(-34.5, 3.1) * mm});
            skLineSegment(sketch, "E220.left", {"start": v(-42.4, 4.4) * mm, "end": v(-42.4, 3.26) * mm});
            skLineSegment(sketch, "E220.right", {"start": v(-34.4, 4.36) * mm, "end": v(-34.4, 3.21) * mm});
            skArc(sketch, "E221.filletArc", {"start": v(-42.3, 4.5) * mm, "mid": v(-42.37, 4.48) * mm, "end": v(-42.4, 4.4) * mm});
            skArc(sketch, "E222.filletArc", {"start": v(-34.4, 4.36) * mm, "mid": v(-34.42, 4.43) * mm, "end": v(-34.5, 4.46) * mm});
            skArc(sketch, "E223.filletArc", {"start": v(-34.5, 3.1) * mm, "mid": v(-34.43, 3.14) * mm, "end": v(-34.4, 3.21) * mm});
            skArc(sketch, "E224.filletArc", {"start": v(-42.4, 3.26) * mm, "mid": v(-42.38, 3.19) * mm, "end": v(-42.3, 3.16) * mm});
            skLineSegment(sketch, "E225.bottom", {"start": v(-42.24, 4.99) * mm, "end": v(-34.5, 4.94) * mm});
            skLineSegment(sketch, "E225.left", {"start": v(-42.24, 4.99) * mm, "end": v(-42.24, 4.5) * mm});
            skLineSegment(sketch, "E225.right", {"start": v(-34.5, 4.94) * mm, "end": v(-34.5, 4.46) * mm});
            skLineSegment(sketch, "E226.bottom", {"start": v(-42.25, 3.16) * mm, "end": v(-34.5, 3.1) * mm});
            skLineSegment(sketch, "E226.top", {"start": v(-42.25, 2.71) * mm, "end": v(-34.5, 2.66) * mm});
            skLineSegment(sketch, "E226.left", {"start": v(-42.25, 3.16) * mm, "end": v(-42.25, 2.71) * mm});
            skLineSegment(sketch, "E226.right", {"start": v(-34.5, 3.1) * mm, "end": v(-34.5, 2.66) * mm});
            skLineSegment(sketch, "E227.bottom", {"start": v(-42.4, 4.26) * mm, "end": v(-42.83, 4.26) * mm});
            skLineSegment(sketch, "E227.top", {"start": v(-42.4, 3.3) * mm, "end": v(-42.83, 3.3) * mm});
            skLineSegment(sketch, "E227.right", {"start": v(-42.83, 4.26) * mm, "end": v(-42.83, 3.3) * mm});
            skLineSegment(sketch, "E228.bottom", {"start": v(-34.4, 4.2) * mm, "end": v(-33.93, 4.2) * mm});
            skLineSegment(sketch, "E228.top", {"start": v(-34.4, 3.26) * mm, "end": v(-33.93, 3.25) * mm});
            skLineSegment(sketch, "E228.right", {"start": v(-33.93, 4.2) * mm, "end": v(-33.93, 3.25) * mm});
            skArc(sketch, "E229", {"start": v(-42.24, 4.66) * mm, "mid": v(-42.5, 4.53) * mm, "end": v(-42.61, 4.26) * mm});
            skArc(sketch, "E230", {"start": v(-42.62, 3.3) * mm, "mid": v(-42.47, 3.06) * mm, "end": v(-42.25, 2.86) * mm});
            skArc(sketch, "E231", {"start": v(-34.07, 4.2) * mm, "mid": v(-34.17, 4.55) * mm, "end": v(-34.5, 4.7) * mm});
            skArc(sketch, "E232", {"start": v(-34.5, 2.89) * mm, "mid": v(-34.3, 3.03) * mm, "end": v(-34.17, 3.26) * mm});
            skLineSegment(sketch, "E233.0", {"start": v(-42.4, 3.3) * mm, "end": v(-33.93, 3.25) * mm, "construction": true});
            skLineSegment(sketch, "E234.0", {"start": v(-42.4, 4.26) * mm, "end": v(-34.4, 4.2) * mm, "construction": true});
            skLineSegment(sketch, "E235.0", {"start": v(-34.5, 2.66) * mm, "end": v(-34.5, 4.46) * mm, "construction": true});
            skLineSegment(sketch, "E236.top", {"start": v(-15.03, 4.18) * mm, "end": v(-10.71, 4.18) * mm});
            skLineSegment(sketch, "E236.left", {"start": v(-15.03, 5.5) * mm, "end": v(-15.03, 4.18) * mm});
            skLineSegment(sketch, "E236.right", {"start": v(-10.71, 5.5) * mm, "end": v(-10.71, 4.18) * mm});
            skLineSegment(sketch, "E237.top", {"start": v(-14.33, 6.25) * mm, "end": v(-11.5, 6.25) * mm});
            skArc(sketch, "E238", {"start": v(-14.33, 6.25) * mm, "mid": v(-14.77, 5.96) * mm, "end": v(-15.03, 5.5) * mm});
            skArc(sketch, "E239", {"start": v(-10.71, 5.5) * mm, "mid": v(-11.04, 5.95) * mm, "end": v(-11.5, 6.25) * mm});
            skArc(sketch, "E240", {"start": v(2.3, 3.19) * mm, "mid": v(0.76, 2.87) * mm, "end": v(-0.52, 1.95) * mm});
            skArc(sketch, "E241", {"start": v(-0.52, 1.95) * mm, "mid": v(-0.82, 1.38) * mm, "end": v(-0.63, 0.75) * mm});
            skLineSegment(sketch, "E242", {"start": v(-0.63, 0.75) * mm, "end": v(0.14, 0.75) * mm});
            skArc(sketch, "E243", {"start": v(0.12, -0.8) * mm, "mid": v(0.27, -0.02) * mm, "end": v(0.14, 0.75) * mm});
            skLineSegment(sketch, "E244", {"start": v(0.12, -0.8) * mm, "end": v(-0.52, -0.8) * mm});
            skArc(sketch, "E245", {"start": v(-0.52, -0.8) * mm, "mid": v(-0.82, -1.47) * mm, "end": v(-0.52, -2.15) * mm});
            skArc(sketch, "E246", {"start": v(-0.52, -2.15) * mm, "mid": v(0.86, -2.6) * mm, "end": v(2.25, -2.99) * mm});
            skSolve(sketch);
        }
        {
            var Q0;
            {var subQ6=sQuery(id+"F4.wireOp",EDGE,"E225.bottom");Q0=makeQuery(id+"F4.imprint","IMPRINT",FACE,{"disambiguationData":[TD([[makeQuery(id+"F4.imprint","IMPRINT",EDGE,{"derivedFrom":subQ6}),1.0]])]});}
            var sketch = newSketch(context, id + "F5", { "sketchPlane" : qUnion([Q0])});
            skLineSegment(sketch, "E247.bottom", {"start": v(-47.98, 0) * mm, "end": v(-2.9, 0) * mm});
            skLineSegment(sketch, "E247.top", {"start": v(-45.33, 7.28) * mm, "end": v(-5.48, 7.28) * mm});
            skLineSegment(sketch, "E247.left", {"start": v(-47.98, 0) * mm, "end": v(-47.98, 6.36) * mm});
            skLineSegment(sketch, "E247.right", {"start": v(-2.9, 0) * mm, "end": v(-2.9, 6.4) * mm});
            skArc(sketch, "E248", {"start": v(-45.33, 7.28) * mm, "mid": v(-46.74, 7.04) * mm, "end": v(-47.98, 6.36) * mm});
            skArc(sketch, "E249", {"start": v(-2.9, 6.4) * mm, "mid": v(-4.12, 7.06) * mm, "end": v(-5.48, 7.28) * mm});
            skLineSegment(sketch, "E250", {"start": v(-47.98, 2.18) * mm, "end": v(-2.9, 2.18) * mm});
            skSolve(sketch);
        }
        {
            var Q0;
            {var subQ6=sQuery(id+"F4.wireOp",EDGE,"E225.bottom");Q0=makeQuery(id+"F4.imprint","IMPRINT",FACE,{"disambiguationData":[TD([[makeQuery(id+"F4.imprint","IMPRINT",EDGE,{"derivedFrom":subQ6}),1.0]])]});}
            var sketch = newSketch(context, id + "F6", { "sketchPlane" : qUnion([Q0])});
            skArc(sketch, "E251", {"start": v(-48.02, 6.33) * mm, "mid": v(-49.56, 6.01) * mm, "end": v(-50.83, 5.1) * mm});
            skArc(sketch, "E252", {"start": v(-50.83, 5.1) * mm, "mid": v(-51.13, 4.52) * mm, "end": v(-50.94, 3.9) * mm});
            skLineSegment(sketch, "E253", {"start": v(-50.94, 3.9) * mm, "end": v(-50.17, 3.9) * mm});
            skArc(sketch, "E254", {"start": v(-50.2, 2.35) * mm, "mid": v(-50.04, 3.12) * mm, "end": v(-50.17, 3.9) * mm});
            skLineSegment(sketch, "E255", {"start": v(-50.2, 2.35) * mm, "end": v(-50.83, 2.35) * mm});
            skArc(sketch, "E256", {"start": v(-50.83, 2.35) * mm, "mid": v(-51.13, 1.67) * mm, "end": v(-50.83, 1) * mm});
            skArc(sketch, "E257", {"start": v(-50.83, 1) * mm, "mid": v(-49.46, 0.54) * mm, "end": v(-48.06, 0.16) * mm});
            skArc(sketch, "E258", {"start": v(-2.88, 6.7) * mm, "mid": v(-2.9, 6.7) * mm, "end": v(-2.94, 6.7) * mm});
            skArc(sketch, "E259", {"start": v(-2.94, 0.53) * mm, "mid": v(-2.93, 0.53) * mm, "end": v(-2.91, 0.53) * mm});
            skArc(sketch, "E260.MirrorCS", {"start": v(-2.92, 6.7) * mm, "mid": v(-1.39, 6.38) * mm, "end": v(-0.11, 5.47) * mm});
            skArc(sketch, "E261.MirrorCS", {"start": v(-0.11, 5.47) * mm, "mid": v(0.19, 4.9) * mm, "end": v(0, 4.27) * mm});
            skLineSegment(sketch, "E262.MirrorCS", {"start": v(0, 4.27) * mm, "end": v(-0.77, 4.27) * mm});
            skArc(sketch, "E263.MirrorCS", {"start": v(-0.75, 2.72) * mm, "mid": v(-0.9, 3.5) * mm, "end": v(-0.77, 4.27) * mm});
            skLineSegment(sketch, "E264.MirrorCS", {"start": v(-0.75, 2.72) * mm, "end": v(-0.11, 2.72) * mm});
            skArc(sketch, "E265.MirrorCS", {"start": v(-0.11, 2.72) * mm, "mid": v(0.19, 2.04) * mm, "end": v(-0.11, 1.37) * mm});
            skArc(sketch, "E266.MirrorCS", {"start": v(-0.11, 1.37) * mm, "mid": v(-1.49, 0.9) * mm, "end": v(-2.88, 0.53) * mm});
            skPoint(sketch, "E267.start.orphan", {"position": v(-5.68, 5.47) * mm});
            skPoint(sketch, "E268.start.orphan", {"position": v(-5.8, 4.27) * mm});
            skPoint(sketch, "E269.end.orphan", {"position": v(-5.03, 4.27) * mm});
            skPoint(sketch, "E270.end.orphan", {"position": v(-5.68, 2.72) * mm});
            skPoint(sketch, "E270.start.orphan", {"position": v(-5.05, 2.72) * mm});
            skPoint(sketch, "E271.orphan", {"position": v(-5.68, 1.37) * mm});
            skPoint(sketch, "E272.trimOffspring.end.orphan", {"position": v(-2.94, 0) * mm});
            skLineSegment(sketch, "E273", {"start": v(-2.88, 6.7) * mm, "end": v(-2.88, 0.53) * mm});
            skLineSegment(sketch, "E274", {"start": v(-48.02, 6.33) * mm, "end": v(-48.06, 0.16) * mm});
            skSolve(sketch);
        }
        {
            var Q0;
            Q0 = qSketchRegion(id + "F4", true);
            extrude(context, id + "F7", {"entities" : qUnion([Q0]), "operationType" : NewBodyOperationType.REMOVE, "oppositeDirection" : true, "depth" : 25.15 * mm});
        }
        {
            var Q0;
            Q0 = qSketchRegion(id + "F5", true);
            extrude(context, id + "F8", {"entities" : qUnion([Q0]), "oppositeDirection" : true, "depth" : 111.5 * mm});
        }
        {
            var Q0;
            Q0 = qSketchRegion(id + "F6", true);
            extrude(context, id + "F9", {"entities" : qUnion([Q0]), "operationType" : NewBodyOperationType.ADD, "oppositeDirection" : true, "depth" : 111.5 * mm});
        }
        {
            var Q0;
            Q0=makeQuery(id+"F8.opExtrude","CAP_FACE",FACE,{"disambiguationData":[OSD([sQuery(id+"F5.wireOp",EDGE,"E247.bottom"),sQuery(id+"F5.wireOp",EDGE,"E247.top"),sQuery(id+"F5.wireOp",EDGE,"E247.left"),sQuery(id+"F5.wireOp",EDGE,"E247.right"),sQuery(id+"F5.wireOp",EDGE,"E248"),sQuery(id+"F5.wireOp",EDGE,"E249")])],"isStart":false});
            var sketch = newSketch(context, id + "F10", { "sketchPlane" : qUnion([Q0])});
            skPoint(sketch, "E275.firstSnap0", {"position": v(-4.12, -7.06) * mm});
            skLineSegment(sketch, "E276.top", {"start": v(-37.15, -3.86) * mm, "end": v(-13.65, -3.86) * mm});
            skLineSegment(sketch, "E276.left", {"start": v(-38.42, -6.62) * mm, "end": v(-38.42, -5.13) * mm});
            skLineSegment(sketch, "E276.right", {"start": v(-12.38, -6.62) * mm, "end": v(-12.38, -5.13) * mm});
            skPoint(sketch, "E277.visualSharp", {"position": v(-38.42, -3.86) * mm});
            skArc(sketch, "E277.filletArc", {"start": v(-37.15, -3.86) * mm, "mid": v(-38.05, -4.24) * mm, "end": v(-38.42, -5.13) * mm});
            skPoint(sketch, "E278.visualSharp", {"position": v(-12.38, -3.86) * mm});
            skArc(sketch, "E278.filletArc", {"start": v(-12.38, -5.13) * mm, "mid": v(-12.75, -4.24) * mm, "end": v(-13.65, -3.86) * mm});
            skLineSegment(sketch, "E279", {"start": v(-38.42, -6.62) * mm, "end": v(-12.38, -6.62) * mm});
            skSolve(sketch);
        }
        {
            var Q0;
            Q0=makeQuery(id+"F10.imprint","IMPRINT",FACE,{"disambiguationData":[TD([[makeQuery(id+"F10.imprint","IMPRINT",EDGE,{"derivedFrom":sQuery(id+"F10.wireOp",EDGE,"E276.top")}),1.0]])]});
            var sketch = newSketch(context, id + "F11", { "sketchPlane" : qUnion([Q0])});
            skLineSegment(sketch, "E280.bottom", {"start": v(-38.38, -6.7) * mm, "end": v(-12.4, -6.7) * mm});
            skLineSegment(sketch, "E280.top", {"start": v(-38.38, -7.31) * mm, "end": v(-12.4, -7.31) * mm});
            skLineSegment(sketch, "E280.left", {"start": v(-38.38, -6.7) * mm, "end": v(-38.38, -7.31) * mm});
            skLineSegment(sketch, "E280.right", {"start": v(-12.4, -6.7) * mm, "end": v(-12.4, -7.31) * mm});
            skSolve(sketch);
        }
        {
            var Q0;
            Q0 = qSketchRegion(id + "F11", true);
            extrude(context, id + "F12", {"entities" : qUnion([Q0]), "operationType" : NewBodyOperationType.REMOVE, "oppositeDirection" : true, "depth" : 11.68 * mm});
        }
    });
